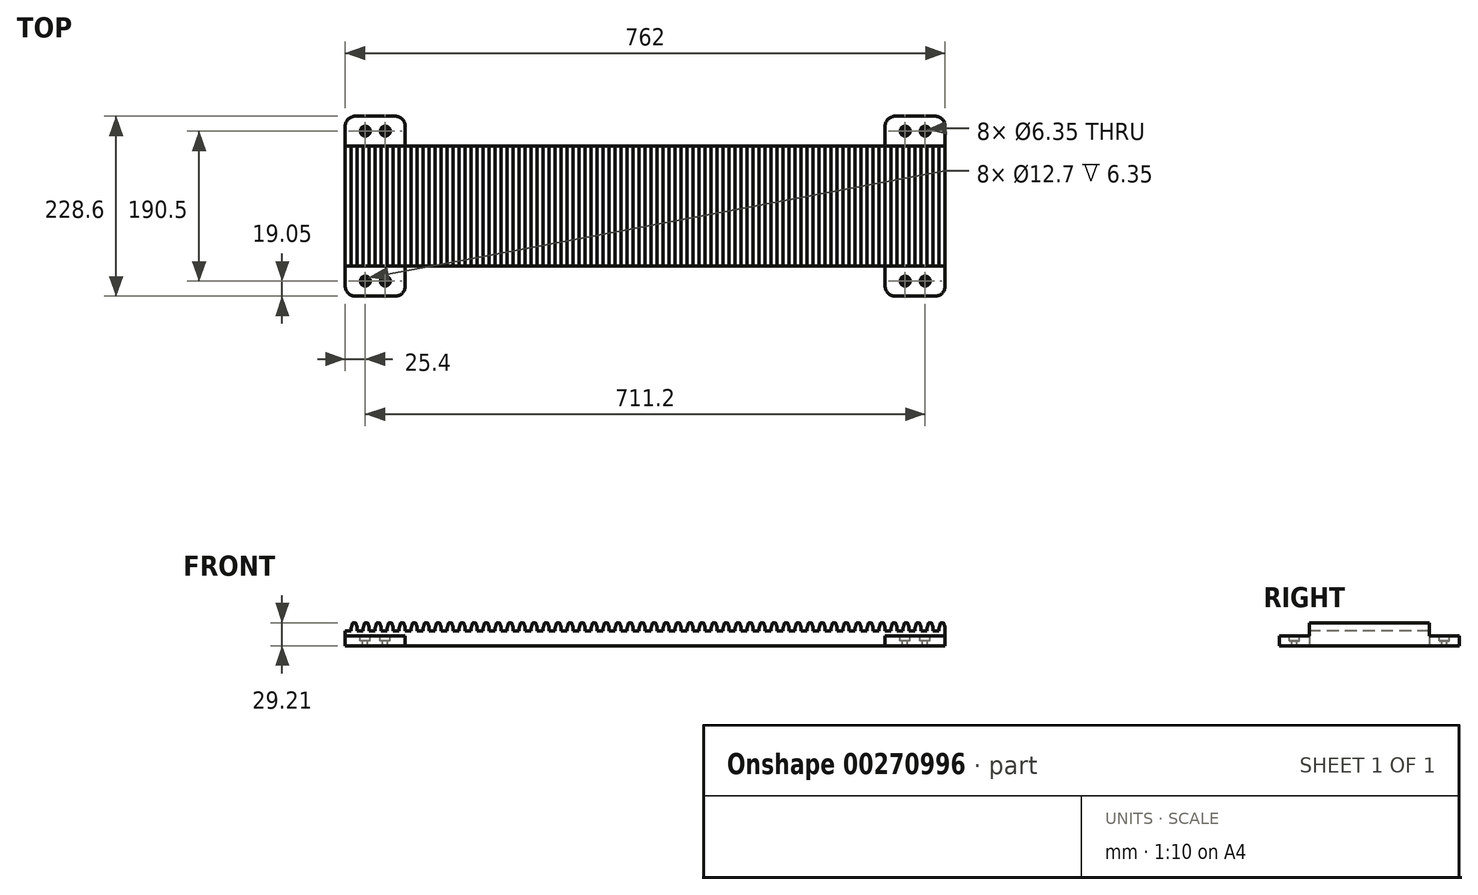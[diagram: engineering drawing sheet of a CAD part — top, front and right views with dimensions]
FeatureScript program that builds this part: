
annotation { "Feature Type Name" : "Feature", "Feature Type Description" : "" }
export const myFeature = defineFeature(function(context is Context, id is Id, definition is map)
    precondition{}
    {
        {
            var Q0;
            Q0=qCreatedBy(makeId("Top.planeOp"),FACE);
            var sketch = newSketch(context, id + "F0", { "sketchPlane" : qUnion([Q0])});
            skLineSegment(sketch, "E0", {"start": v(0, 12.7) * mm, "end": v(0, 215.9) * mm});
            skLineSegment(sketch, "E1", {"start": v(12.7, 228.6) * mm, "end": v(63.5, 228.6) * mm});
            skLineSegment(sketch, "E2", {"start": v(76.2, 215.9) * mm, "end": v(76.2, 190.5) * mm});
            skLineSegment(sketch, "E3", {"start": v(76.2, 190.5) * mm, "end": v(381, 190.5) * mm});
            skLineSegment(sketch, "E4", {"start": v(12.7, 0) * mm, "end": v(63.5, 0) * mm});
            skLineSegment(sketch, "E5", {"start": v(76.2, 12.7) * mm, "end": v(76.2, 38.1) * mm});
            skPoint(sketch, "E5.endSnap0", {"position": v(76.2, 209.55) * mm});
            skLineSegment(sketch, "E6", {"start": v(76.2, 38.1) * mm, "end": v(381, 38.1) * mm});
            skLineSegment(sketch, "E7", {"start": v(381, 190.5) * mm, "end": v(381, 38.1) * mm, "construction": true});
            skPoint(sketch, "E8.visualSharp", {"position": v(76.2, 228.6) * mm});
            skArc(sketch, "E8.filletArc", {"start": v(76.2, 215.9) * mm, "mid": v(72.48, 224.88) * mm, "end": v(63.5, 228.6) * mm});
            skPoint(sketch, "E9.visualSharp", {"position": v(0, 228.6) * mm});
            skArc(sketch, "E9.filletArc", {"start": v(12.7, 228.6) * mm, "mid": v(3.72, 224.88) * mm, "end": v(0, 215.9) * mm});
            skPoint(sketch, "E10.visualSharp", {"position": v(0, 0) * mm});
            skArc(sketch, "E10.filletArc", {"start": v(0, 12.7) * mm, "mid": v(3.72, 3.72) * mm, "end": v(12.7, 0) * mm});
            skPoint(sketch, "E11.visualSharp", {"position": v(76.2, 0) * mm});
            skArc(sketch, "E11.filletArc", {"start": v(63.5, 0) * mm, "mid": v(72.48, 3.72) * mm, "end": v(76.2, 12.7) * mm});
            skArc(sketch, "E12.MirrorCS", {"start": v(762, 12.7) * mm, "mid": v(758.28, 3.72) * mm, "end": v(749.3, 0) * mm});
            skArc(sketch, "E13.MirrorCS", {"start": v(749.3, 228.6) * mm, "mid": v(758.28, 224.88) * mm, "end": v(762, 215.9) * mm});
            skArc(sketch, "E14.MirrorCS", {"start": v(685.8, 215.9) * mm, "mid": v(689.52, 224.88) * mm, "end": v(698.5, 228.6) * mm});
            skArc(sketch, "E15.MirrorCS", {"start": v(698.5, 0) * mm, "mid": v(689.52, 3.72) * mm, "end": v(685.8, 12.7) * mm});
            skLineSegment(sketch, "E16.MirrorCS", {"start": v(685.8, 215.9) * mm, "end": v(685.8, 190.5) * mm});
            skPoint(sketch, "E17.MirrorP", {"position": v(685.8, 209.55) * mm});
            skPoint(sketch, "E18.MirrorP", {"position": v(685.8, 0) * mm});
            skLineSegment(sketch, "E19.MirrorCS", {"start": v(762, 12.7) * mm, "end": v(762, 215.9) * mm});
            skPoint(sketch, "E20.MirrorP", {"position": v(762, 228.6) * mm});
            skPoint(sketch, "E21.MirrorP", {"position": v(685.8, 228.6) * mm});
            skLineSegment(sketch, "E22.MirrorCS", {"start": v(749.3, 228.6) * mm, "end": v(698.5, 228.6) * mm});
            skPoint(sketch, "E23.MirrorP", {"position": v(762, 0) * mm});
            skLineSegment(sketch, "E24.MirrorCS", {"start": v(749.3, 0) * mm, "end": v(698.5, 0) * mm});
            skLineSegment(sketch, "E25.MirrorCS", {"start": v(685.8, 38.1) * mm, "end": v(381, 38.1) * mm});
            skLineSegment(sketch, "E26.MirrorCS", {"start": v(685.8, 190.5) * mm, "end": v(381, 190.5) * mm});
            skLineSegment(sketch, "E27.MirrorCS", {"start": v(685.8, 12.7) * mm, "end": v(685.8, 38.1) * mm});
            skPoint(sketch, "E28", {"position": v(25.4, 209.55) * mm});
            skPoint(sketch, "E29", {"position": v(50.8, 209.55) * mm});
            skLineSegment(sketch, "E30", {"start": v(0, 114.3) * mm, "end": v(762, 114.3) * mm, "construction": true});
            skPoint(sketch, "E31.MirrorP", {"position": v(50.8, 19.05) * mm});
            skPoint(sketch, "E32.MirrorP", {"position": v(25.4, 19.05) * mm});
            skPoint(sketch, "E33.MirrorP", {"position": v(736.6, 209.55) * mm});
            skPoint(sketch, "E34.MirrorP", {"position": v(711.2, 209.55) * mm});
            skPoint(sketch, "E35.MirrorP", {"position": v(711.2, 19.05) * mm});
            skPoint(sketch, "E36.MirrorP", {"position": v(736.6, 19.05) * mm});
            skSolve(sketch);
        }
        {
            var Q0;
            Q0 = qSketchRegion(id + "F0", true);
            extrude(context, id + "F1", {"entities" : qUnion([Q0]), "depth" : 12.7 * mm});
        }
        {
            var Q0;
            Q0=makeQuery(id+"F1.opExtrude","CAP_FACE",FACE,{"disambiguationData":[OSD([sQuery(id+"F0.wireOp",EDGE,"E0"),sQuery(id+"F0.wireOp",EDGE,"E1"),sQuery(id+"F0.wireOp",EDGE,"E2"),sQuery(id+"F0.wireOp",EDGE,"E3"),sQuery(id+"F0.wireOp",EDGE,"E4"),sQuery(id+"F0.wireOp",EDGE,"E5"),sQuery(id+"F0.wireOp",EDGE,"E6"),sQuery(id+"F0.wireOp",EDGE,"E8.filletArc"),sQuery(id+"F0.wireOp",EDGE,"E9.filletArc"),sQuery(id+"F0.wireOp",EDGE,"E10.filletArc"),sQuery(id+"F0.wireOp",EDGE,"E11.filletArc"),sQuery(id+"F0.wireOp",EDGE,"E12.MirrorCS"),sQuery(id+"F0.wireOp",EDGE,"E13.MirrorCS"),sQuery(id+"F0.wireOp",EDGE,"E14.MirrorCS"),sQuery(id+"F0.wireOp",EDGE,"E15.MirrorCS"),sQuery(id+"F0.wireOp",EDGE,"E16.MirrorCS"),sQuery(id+"F0.wireOp",EDGE,"E19.MirrorCS"),sQuery(id+"F0.wireOp",EDGE,"E22.MirrorCS"),sQuery(id+"F0.wireOp",EDGE,"E24.MirrorCS"),sQuery(id+"F0.wireOp",EDGE,"E25.MirrorCS"),sQuery(id+"F0.wireOp",EDGE,"E26.MirrorCS"),sQuery(id+"F0.wireOp",EDGE,"E27.MirrorCS")])],"isStart":false});
            var sketch = newSketch(context, id + "F2", { "sketchPlane" : qUnion([Q0])});
            skLineSegment(sketch, "E37", {"start": v(0, 190.5) * mm, "end": v(762, 190.5) * mm});
            skLineSegment(sketch, "E38", {"start": v(762, 190.5) * mm, "end": v(762, 38.1) * mm});
            skLineSegment(sketch, "E39", {"start": v(762, 38.1) * mm, "end": v(0, 38.1) * mm});
            skPoint(sketch, "E39.endSnap0", {"position": v(0, 114.3) * mm});
            skLineSegment(sketch, "E40", {"start": v(0, 38.1) * mm, "end": v(0, 190.5) * mm});
            skPoint(sketch, "E41", {"position": v(25.4, 209.55) * mm});
            skPoint(sketch, "E42", {"position": v(50.8, 209.55) * mm});
            skPoint(sketch, "E43.MirrorP", {"position": v(25.4, 19.05) * mm});
            skPoint(sketch, "E44.MirrorP", {"position": v(50.8, 19.05) * mm});
            skPoint(sketch, "E45.MirrorP", {"position": v(711.2, 209.55) * mm});
            skPoint(sketch, "E46.MirrorP", {"position": v(736.6, 209.55) * mm});
            skPoint(sketch, "E47.MirrorP", {"position": v(736.6, 19.05) * mm});
            skPoint(sketch, "E48.MirrorP", {"position": v(711.2, 19.05) * mm});
            skSolve(sketch);
        }
        {
            var Q0;
            Q0 = qSketchRegion(id + "F2", true);
            extrude(context, id + "F3", {"entities" : qUnion([Q0]), "operationType" : NewBodyOperationType.ADD, "depth" : 6.35 * mm});
        }
        {
            var Q0;
            Q0=sQuery(id+"F2.wireOp",VERTEX,"E46.MirrorP");
            var Q1;
            Q1=sQuery(id+"F2.wireOp",VERTEX,"E45.MirrorP");
            var Q2;
            Q2=sQuery(id+"F2.wireOp",VERTEX,"E47.MirrorP");
            var Q3;
            Q3=sQuery(id+"F2.wireOp",VERTEX,"E48.MirrorP");
            var Q4;
            Q4=sQuery(id+"F2.wireOp",VERTEX,"E42");
            var Q5;
            Q5=sQuery(id+"F2.wireOp",VERTEX,"E41");
            var Q6;
            Q6=sQuery(id+"F2.wireOp",VERTEX,"E44.MirrorP");
            var Q7;
            Q7=sQuery(id+"F2.wireOp",VERTEX,"E43.MirrorP");
            var Q8;
            Q8=makeQuery(id+"F1.opExtrude","SWEPT_BODY",BODY,{"disambiguationData":[OSD([sQuery(id+"F0.wireOp",EDGE,"E0"),sQuery(id+"F0.wireOp",EDGE,"E1"),sQuery(id+"F0.wireOp",EDGE,"E2"),sQuery(id+"F0.wireOp",EDGE,"E3"),sQuery(id+"F0.wireOp",EDGE,"E4"),sQuery(id+"F0.wireOp",EDGE,"E5"),sQuery(id+"F0.wireOp",EDGE,"E6"),sQuery(id+"F0.wireOp",EDGE,"E8.filletArc"),sQuery(id+"F0.wireOp",EDGE,"E9.filletArc"),sQuery(id+"F0.wireOp",EDGE,"E10.filletArc"),sQuery(id+"F0.wireOp",EDGE,"E11.filletArc"),sQuery(id+"F0.wireOp",EDGE,"E12.MirrorCS"),sQuery(id+"F0.wireOp",EDGE,"E13.MirrorCS"),sQuery(id+"F0.wireOp",EDGE,"E14.MirrorCS"),sQuery(id+"F0.wireOp",EDGE,"E15.MirrorCS"),sQuery(id+"F0.wireOp",EDGE,"E16.MirrorCS"),sQuery(id+"F0.wireOp",EDGE,"E19.MirrorCS"),sQuery(id+"F0.wireOp",EDGE,"E22.MirrorCS"),sQuery(id+"F0.wireOp",EDGE,"E24.MirrorCS"),sQuery(id+"F0.wireOp",EDGE,"E25.MirrorCS"),sQuery(id+"F0.wireOp",EDGE,"E26.MirrorCS"),sQuery(id+"F0.wireOp",EDGE,"E27.MirrorCS")])]});
            hole(context, id + "F4", {"style" : HoleStyle.C_BORE, "endStyle" : HoleEndStyle.THROUGH, "holeDiameter" : 6.35 * mm, "cBoreDiameter" : 12.7 * mm, "cBoreDepth" : 6.35 * mm, "tappedDepth" : 12.7 * mm, "tapClearance" : 3, "locations" : qUnion([Q0, Q1, Q2, Q3, Q4, Q5, Q6, Q7]), "scope" : qUnion([Q8])});
        }
        {
            var Q0;
            Q0=makeQuery(id+"F3.opExtrude","CAP_FACE",FACE,{"disambiguationData":[OSD([sQuery(id+"F2.wireOp",EDGE,"E37"),sQuery(id+"F2.wireOp",EDGE,"E38"),sQuery(id+"F2.wireOp",EDGE,"E39"),sQuery(id+"F2.wireOp",EDGE,"E40")])],"isStart":false});
            var sketch = newSketch(context, id + "F5", { "sketchPlane" : qUnion([Q0])});
            skLineSegment(sketch, "E49", {"start": v(7.62, 190.5) * mm, "end": v(7.62, 38.1) * mm});
            skLineSegment(sketch, "E50.0", {"start": v(15.24, 190.5) * mm, "end": v(15.24, 38.1) * mm});
            skLineSegment(sketch, "E51", {"start": v(15.24, 190.5) * mm, "end": v(7.62, 190.5) * mm});
            skLineSegment(sketch, "E52.0", {"start": v(22.86, 190.5) * mm, "end": v(22.86, 38.1) * mm});
            skLineSegment(sketch, "E53.0", {"start": v(30.48, 190.5) * mm, "end": v(30.48, 38.1) * mm});
            skLineSegment(sketch, "E54", {"start": v(22.86, 190.5) * mm, "end": v(30.48, 190.5) * mm});
            skLineSegment(sketch, "E55", {"start": v(22.86, 38.1) * mm, "end": v(30.48, 38.1) * mm});
            skLineSegment(sketch, "E56", {"start": v(7.62, 38.1) * mm, "end": v(15.24, 38.1) * mm});
            skLineSegment(sketch, "E57.1.0.0", {"start": v(45.72, 190.5) * mm, "end": v(38.1, 190.5) * mm});
            skLineSegment(sketch, "E57.1.0.1", {"start": v(38.1, 190.5) * mm, "end": v(38.1, 38.1) * mm});
            skLineSegment(sketch, "E57.1.0.2", {"start": v(45.72, 190.5) * mm, "end": v(45.72, 38.1) * mm});
            skLineSegment(sketch, "E57.1.0.3", {"start": v(53.34, 190.5) * mm, "end": v(53.34, 38.1) * mm});
            skLineSegment(sketch, "E57.1.0.4", {"start": v(53.34, 190.5) * mm, "end": v(60.96, 190.5) * mm});
            skLineSegment(sketch, "E57.1.0.5", {"start": v(60.96, 190.5) * mm, "end": v(60.96, 38.1) * mm});
            skLineSegment(sketch, "E57.1.0.6", {"start": v(53.34, 38.1) * mm, "end": v(60.96, 38.1) * mm});
            skLineSegment(sketch, "E57.1.0.7", {"start": v(38.1, 38.1) * mm, "end": v(45.72, 38.1) * mm});
            skLineSegment(sketch, "E57.2.0.0", {"start": v(76.2, 190.5) * mm, "end": v(68.58, 190.5) * mm});
            skLineSegment(sketch, "E57.2.0.1", {"start": v(68.58, 190.5) * mm, "end": v(68.58, 38.1) * mm});
            skLineSegment(sketch, "E57.2.0.2", {"start": v(76.2, 190.5) * mm, "end": v(76.2, 38.1) * mm});
            skLineSegment(sketch, "E57.2.0.3", {"start": v(83.82, 190.5) * mm, "end": v(83.82, 38.1) * mm});
            skLineSegment(sketch, "E57.2.0.4", {"start": v(83.82, 190.5) * mm, "end": v(91.44, 190.5) * mm});
            skLineSegment(sketch, "E57.2.0.5", {"start": v(91.44, 190.5) * mm, "end": v(91.44, 38.1) * mm});
            skLineSegment(sketch, "E57.2.0.6", {"start": v(83.82, 38.1) * mm, "end": v(91.44, 38.1) * mm});
            skLineSegment(sketch, "E57.2.0.7", {"start": v(68.58, 38.1) * mm, "end": v(76.2, 38.1) * mm});
            skLineSegment(sketch, "E57.3.0.0", {"start": v(106.68, 190.5) * mm, "end": v(99.06, 190.5) * mm});
            skLineSegment(sketch, "E57.3.0.1", {"start": v(99.06, 190.5) * mm, "end": v(99.06, 38.1) * mm});
            skLineSegment(sketch, "E57.3.0.2", {"start": v(106.68, 190.5) * mm, "end": v(106.68, 38.1) * mm});
            skLineSegment(sketch, "E57.3.0.3", {"start": v(114.3, 190.5) * mm, "end": v(114.3, 38.1) * mm});
            skLineSegment(sketch, "E57.3.0.4", {"start": v(114.3, 190.5) * mm, "end": v(121.92, 190.5) * mm});
            skLineSegment(sketch, "E57.3.0.5", {"start": v(121.92, 190.5) * mm, "end": v(121.92, 38.1) * mm});
            skLineSegment(sketch, "E57.3.0.6", {"start": v(114.3, 38.1) * mm, "end": v(121.92, 38.1) * mm});
            skLineSegment(sketch, "E57.3.0.7", {"start": v(99.06, 38.1) * mm, "end": v(106.68, 38.1) * mm});
            skLineSegment(sketch, "E57.4.0.0", {"start": v(137.16, 190.5) * mm, "end": v(129.54, 190.5) * mm});
            skLineSegment(sketch, "E57.4.0.1", {"start": v(129.54, 190.5) * mm, "end": v(129.54, 38.1) * mm});
            skLineSegment(sketch, "E57.4.0.2", {"start": v(137.16, 190.5) * mm, "end": v(137.16, 38.1) * mm});
            skLineSegment(sketch, "E57.4.0.3", {"start": v(144.78, 190.5) * mm, "end": v(144.78, 38.1) * mm});
            skLineSegment(sketch, "E57.4.0.4", {"start": v(144.78, 190.5) * mm, "end": v(152.4, 190.5) * mm});
            skLineSegment(sketch, "E57.4.0.5", {"start": v(152.4, 190.5) * mm, "end": v(152.4, 38.1) * mm});
            skLineSegment(sketch, "E57.4.0.6", {"start": v(144.78, 38.1) * mm, "end": v(152.4, 38.1) * mm});
            skLineSegment(sketch, "E57.4.0.7", {"start": v(129.54, 38.1) * mm, "end": v(137.16, 38.1) * mm});
            skLineSegment(sketch, "E57.5.0.0", {"start": v(167.64, 190.5) * mm, "end": v(160.02, 190.5) * mm});
            skLineSegment(sketch, "E57.5.0.1", {"start": v(160.02, 190.5) * mm, "end": v(160.02, 38.1) * mm});
            skLineSegment(sketch, "E57.5.0.2", {"start": v(167.64, 190.5) * mm, "end": v(167.64, 38.1) * mm});
            skLineSegment(sketch, "E57.5.0.3", {"start": v(175.26, 190.5) * mm, "end": v(175.26, 38.1) * mm});
            skLineSegment(sketch, "E57.5.0.4", {"start": v(175.26, 190.5) * mm, "end": v(182.88, 190.5) * mm});
            skLineSegment(sketch, "E57.5.0.5", {"start": v(182.88, 190.5) * mm, "end": v(182.88, 38.1) * mm});
            skLineSegment(sketch, "E57.5.0.6", {"start": v(175.26, 38.1) * mm, "end": v(182.88, 38.1) * mm});
            skLineSegment(sketch, "E57.5.0.7", {"start": v(160.02, 38.1) * mm, "end": v(167.64, 38.1) * mm});
            skLineSegment(sketch, "E57.6.0.0", {"start": v(198.12, 190.5) * mm, "end": v(190.5, 190.5) * mm});
            skLineSegment(sketch, "E57.6.0.1", {"start": v(190.5, 190.5) * mm, "end": v(190.5, 38.1) * mm});
            skLineSegment(sketch, "E57.6.0.2", {"start": v(198.12, 190.5) * mm, "end": v(198.12, 38.1) * mm});
            skLineSegment(sketch, "E57.6.0.3", {"start": v(205.74, 190.5) * mm, "end": v(205.74, 38.1) * mm});
            skLineSegment(sketch, "E57.6.0.4", {"start": v(205.74, 190.5) * mm, "end": v(213.36, 190.5) * mm});
            skLineSegment(sketch, "E57.6.0.5", {"start": v(213.36, 190.5) * mm, "end": v(213.36, 38.1) * mm});
            skLineSegment(sketch, "E57.6.0.6", {"start": v(205.74, 38.1) * mm, "end": v(213.36, 38.1) * mm});
            skLineSegment(sketch, "E57.6.0.7", {"start": v(190.5, 38.1) * mm, "end": v(198.12, 38.1) * mm});
            skLineSegment(sketch, "E57.7.0.0", {"start": v(228.6, 190.5) * mm, "end": v(220.98, 190.5) * mm});
            skLineSegment(sketch, "E57.7.0.1", {"start": v(220.98, 190.5) * mm, "end": v(220.98, 38.1) * mm});
            skLineSegment(sketch, "E57.7.0.2", {"start": v(228.6, 190.5) * mm, "end": v(228.6, 38.1) * mm});
            skLineSegment(sketch, "E57.7.0.3", {"start": v(236.22, 190.5) * mm, "end": v(236.22, 38.1) * mm});
            skLineSegment(sketch, "E57.7.0.4", {"start": v(236.22, 190.5) * mm, "end": v(243.84, 190.5) * mm});
            skLineSegment(sketch, "E57.7.0.5", {"start": v(243.84, 190.5) * mm, "end": v(243.84, 38.1) * mm});
            skLineSegment(sketch, "E57.7.0.6", {"start": v(236.22, 38.1) * mm, "end": v(243.84, 38.1) * mm});
            skLineSegment(sketch, "E57.7.0.7", {"start": v(220.98, 38.1) * mm, "end": v(228.6, 38.1) * mm});
            skLineSegment(sketch, "E57.8.0.0", {"start": v(259.08, 190.5) * mm, "end": v(251.46, 190.5) * mm});
            skLineSegment(sketch, "E57.8.0.1", {"start": v(251.46, 190.5) * mm, "end": v(251.46, 38.1) * mm});
            skLineSegment(sketch, "E57.8.0.2", {"start": v(259.08, 190.5) * mm, "end": v(259.08, 38.1) * mm});
            skLineSegment(sketch, "E57.8.0.3", {"start": v(266.7, 190.5) * mm, "end": v(266.7, 38.1) * mm});
            skLineSegment(sketch, "E57.8.0.4", {"start": v(266.7, 190.5) * mm, "end": v(274.32, 190.5) * mm});
            skLineSegment(sketch, "E57.8.0.5", {"start": v(274.32, 190.5) * mm, "end": v(274.32, 38.1) * mm});
            skLineSegment(sketch, "E57.8.0.6", {"start": v(266.7, 38.1) * mm, "end": v(274.32, 38.1) * mm});
            skLineSegment(sketch, "E57.8.0.7", {"start": v(251.46, 38.1) * mm, "end": v(259.08, 38.1) * mm});
            skLineSegment(sketch, "E57.9.0.0", {"start": v(289.56, 190.5) * mm, "end": v(281.94, 190.5) * mm});
            skLineSegment(sketch, "E57.9.0.1", {"start": v(281.94, 190.5) * mm, "end": v(281.94, 38.1) * mm});
            skLineSegment(sketch, "E57.9.0.2", {"start": v(289.56, 190.5) * mm, "end": v(289.56, 38.1) * mm});
            skLineSegment(sketch, "E57.9.0.3", {"start": v(297.18, 190.5) * mm, "end": v(297.18, 38.1) * mm});
            skLineSegment(sketch, "E57.9.0.4", {"start": v(297.18, 190.5) * mm, "end": v(304.8, 190.5) * mm});
            skLineSegment(sketch, "E57.9.0.5", {"start": v(304.8, 190.5) * mm, "end": v(304.8, 38.1) * mm});
            skLineSegment(sketch, "E57.9.0.6", {"start": v(297.18, 38.1) * mm, "end": v(304.8, 38.1) * mm});
            skLineSegment(sketch, "E57.9.0.7", {"start": v(281.94, 38.1) * mm, "end": v(289.56, 38.1) * mm});
            skLineSegment(sketch, "E57.10.0.0", {"start": v(320.04, 190.5) * mm, "end": v(312.42, 190.5) * mm});
            skLineSegment(sketch, "E57.10.0.1", {"start": v(312.42, 190.5) * mm, "end": v(312.42, 38.1) * mm});
            skLineSegment(sketch, "E57.10.0.2", {"start": v(320.04, 190.5) * mm, "end": v(320.04, 38.1) * mm});
            skLineSegment(sketch, "E57.10.0.3", {"start": v(327.66, 190.5) * mm, "end": v(327.66, 38.1) * mm});
            skLineSegment(sketch, "E57.10.0.4", {"start": v(327.66, 190.5) * mm, "end": v(335.28, 190.5) * mm});
            skLineSegment(sketch, "E57.10.0.5", {"start": v(335.28, 190.5) * mm, "end": v(335.28, 38.1) * mm});
            skLineSegment(sketch, "E57.10.0.6", {"start": v(327.66, 38.1) * mm, "end": v(335.28, 38.1) * mm});
            skLineSegment(sketch, "E57.10.0.7", {"start": v(312.42, 38.1) * mm, "end": v(320.04, 38.1) * mm});
            skLineSegment(sketch, "E57.11.0.0", {"start": v(350.52, 190.5) * mm, "end": v(342.9, 190.5) * mm});
            skLineSegment(sketch, "E57.11.0.1", {"start": v(342.9, 190.5) * mm, "end": v(342.9, 38.1) * mm});
            skLineSegment(sketch, "E57.11.0.2", {"start": v(350.52, 190.5) * mm, "end": v(350.52, 38.1) * mm});
            skLineSegment(sketch, "E57.11.0.3", {"start": v(358.14, 190.5) * mm, "end": v(358.14, 38.1) * mm});
            skLineSegment(sketch, "E57.11.0.4", {"start": v(358.14, 190.5) * mm, "end": v(365.76, 190.5) * mm});
            skLineSegment(sketch, "E57.11.0.5", {"start": v(365.76, 190.5) * mm, "end": v(365.76, 38.1) * mm});
            skLineSegment(sketch, "E57.11.0.6", {"start": v(358.14, 38.1) * mm, "end": v(365.76, 38.1) * mm});
            skLineSegment(sketch, "E57.11.0.7", {"start": v(342.9, 38.1) * mm, "end": v(350.52, 38.1) * mm});
            skLineSegment(sketch, "E57.12.0.0", {"start": v(381, 190.5) * mm, "end": v(373.38, 190.5) * mm});
            skLineSegment(sketch, "E57.12.0.1", {"start": v(373.38, 190.5) * mm, "end": v(373.38, 38.1) * mm});
            skLineSegment(sketch, "E57.12.0.2", {"start": v(381, 190.5) * mm, "end": v(381, 38.1) * mm});
            skLineSegment(sketch, "E57.12.0.3", {"start": v(388.62, 190.5) * mm, "end": v(388.62, 38.1) * mm});
            skLineSegment(sketch, "E57.12.0.4", {"start": v(388.62, 190.5) * mm, "end": v(396.24, 190.5) * mm});
            skLineSegment(sketch, "E57.12.0.5", {"start": v(396.24, 190.5) * mm, "end": v(396.24, 38.1) * mm});
            skLineSegment(sketch, "E57.12.0.6", {"start": v(388.62, 38.1) * mm, "end": v(396.24, 38.1) * mm});
            skLineSegment(sketch, "E57.12.0.7", {"start": v(373.38, 38.1) * mm, "end": v(381, 38.1) * mm});
            skLineSegment(sketch, "E57.13.0.0", {"start": v(411.48, 190.5) * mm, "end": v(403.86, 190.5) * mm});
            skLineSegment(sketch, "E57.13.0.1", {"start": v(403.86, 190.5) * mm, "end": v(403.86, 38.1) * mm});
            skLineSegment(sketch, "E57.13.0.2", {"start": v(411.48, 190.5) * mm, "end": v(411.48, 38.1) * mm});
            skLineSegment(sketch, "E57.13.0.3", {"start": v(419.1, 190.5) * mm, "end": v(419.1, 38.1) * mm});
            skLineSegment(sketch, "E57.13.0.4", {"start": v(419.1, 190.5) * mm, "end": v(426.72, 190.5) * mm});
            skLineSegment(sketch, "E57.13.0.5", {"start": v(426.72, 190.5) * mm, "end": v(426.72, 38.1) * mm});
            skLineSegment(sketch, "E57.13.0.6", {"start": v(419.1, 38.1) * mm, "end": v(426.72, 38.1) * mm});
            skLineSegment(sketch, "E57.13.0.7", {"start": v(403.86, 38.1) * mm, "end": v(411.48, 38.1) * mm});
            skLineSegment(sketch, "E57.14.0.0", {"start": v(441.96, 190.5) * mm, "end": v(434.34, 190.5) * mm});
            skLineSegment(sketch, "E57.14.0.1", {"start": v(434.34, 190.5) * mm, "end": v(434.34, 38.1) * mm});
            skLineSegment(sketch, "E57.14.0.2", {"start": v(441.96, 190.5) * mm, "end": v(441.96, 38.1) * mm});
            skLineSegment(sketch, "E57.14.0.3", {"start": v(449.58, 190.5) * mm, "end": v(449.58, 38.1) * mm});
            skLineSegment(sketch, "E57.14.0.4", {"start": v(449.58, 190.5) * mm, "end": v(457.2, 190.5) * mm});
            skLineSegment(sketch, "E57.14.0.5", {"start": v(457.2, 190.5) * mm, "end": v(457.2, 38.1) * mm});
            skLineSegment(sketch, "E57.14.0.6", {"start": v(449.58, 38.1) * mm, "end": v(457.2, 38.1) * mm});
            skLineSegment(sketch, "E57.14.0.7", {"start": v(434.34, 38.1) * mm, "end": v(441.96, 38.1) * mm});
            skLineSegment(sketch, "E57.15.0.0", {"start": v(472.44, 190.5) * mm, "end": v(464.82, 190.5) * mm});
            skLineSegment(sketch, "E57.15.0.1", {"start": v(464.82, 190.5) * mm, "end": v(464.82, 38.1) * mm});
            skLineSegment(sketch, "E57.15.0.2", {"start": v(472.44, 190.5) * mm, "end": v(472.44, 38.1) * mm});
            skLineSegment(sketch, "E57.15.0.3", {"start": v(480.06, 190.5) * mm, "end": v(480.06, 38.1) * mm});
            skLineSegment(sketch, "E57.15.0.4", {"start": v(480.06, 190.5) * mm, "end": v(487.68, 190.5) * mm});
            skLineSegment(sketch, "E57.15.0.5", {"start": v(487.68, 190.5) * mm, "end": v(487.68, 38.1) * mm});
            skLineSegment(sketch, "E57.15.0.6", {"start": v(480.06, 38.1) * mm, "end": v(487.68, 38.1) * mm});
            skLineSegment(sketch, "E57.15.0.7", {"start": v(464.82, 38.1) * mm, "end": v(472.44, 38.1) * mm});
            skLineSegment(sketch, "E57.16.0.0", {"start": v(502.92, 190.5) * mm, "end": v(495.3, 190.5) * mm});
            skLineSegment(sketch, "E57.16.0.1", {"start": v(495.3, 190.5) * mm, "end": v(495.3, 38.1) * mm});
            skLineSegment(sketch, "E57.16.0.2", {"start": v(502.92, 190.5) * mm, "end": v(502.92, 38.1) * mm});
            skLineSegment(sketch, "E57.16.0.3", {"start": v(510.54, 190.5) * mm, "end": v(510.54, 38.1) * mm});
            skLineSegment(sketch, "E57.16.0.4", {"start": v(510.54, 190.5) * mm, "end": v(518.16, 190.5) * mm});
            skLineSegment(sketch, "E57.16.0.5", {"start": v(518.16, 190.5) * mm, "end": v(518.16, 38.1) * mm});
            skLineSegment(sketch, "E57.16.0.6", {"start": v(510.54, 38.1) * mm, "end": v(518.16, 38.1) * mm});
            skLineSegment(sketch, "E57.16.0.7", {"start": v(495.3, 38.1) * mm, "end": v(502.92, 38.1) * mm});
            skLineSegment(sketch, "E57.17.0.0", {"start": v(533.4, 190.5) * mm, "end": v(525.78, 190.5) * mm});
            skLineSegment(sketch, "E57.17.0.1", {"start": v(525.78, 190.5) * mm, "end": v(525.78, 38.1) * mm});
            skLineSegment(sketch, "E57.17.0.2", {"start": v(533.4, 190.5) * mm, "end": v(533.4, 38.1) * mm});
            skLineSegment(sketch, "E57.17.0.3", {"start": v(541.02, 190.5) * mm, "end": v(541.02, 38.1) * mm});
            skLineSegment(sketch, "E57.17.0.4", {"start": v(541.02, 190.5) * mm, "end": v(548.64, 190.5) * mm});
            skLineSegment(sketch, "E57.17.0.5", {"start": v(548.64, 190.5) * mm, "end": v(548.64, 38.1) * mm});
            skLineSegment(sketch, "E57.17.0.6", {"start": v(541.02, 38.1) * mm, "end": v(548.64, 38.1) * mm});
            skLineSegment(sketch, "E57.17.0.7", {"start": v(525.78, 38.1) * mm, "end": v(533.4, 38.1) * mm});
            skLineSegment(sketch, "E57.18.0.0", {"start": v(563.88, 190.5) * mm, "end": v(556.26, 190.5) * mm});
            skLineSegment(sketch, "E57.18.0.1", {"start": v(556.26, 190.5) * mm, "end": v(556.26, 38.1) * mm});
            skLineSegment(sketch, "E57.18.0.2", {"start": v(563.88, 190.5) * mm, "end": v(563.88, 38.1) * mm});
            skLineSegment(sketch, "E57.18.0.3", {"start": v(571.5, 190.5) * mm, "end": v(571.5, 38.1) * mm});
            skLineSegment(sketch, "E57.18.0.4", {"start": v(571.5, 190.5) * mm, "end": v(579.12, 190.5) * mm});
            skLineSegment(sketch, "E57.18.0.5", {"start": v(579.12, 190.5) * mm, "end": v(579.12, 38.1) * mm});
            skLineSegment(sketch, "E57.18.0.6", {"start": v(571.5, 38.1) * mm, "end": v(579.12, 38.1) * mm});
            skLineSegment(sketch, "E57.18.0.7", {"start": v(556.26, 38.1) * mm, "end": v(563.88, 38.1) * mm});
            skLineSegment(sketch, "E57.19.0.0", {"start": v(594.36, 190.5) * mm, "end": v(586.74, 190.5) * mm});
            skLineSegment(sketch, "E57.19.0.1", {"start": v(586.74, 190.5) * mm, "end": v(586.74, 38.1) * mm});
            skLineSegment(sketch, "E57.19.0.2", {"start": v(594.36, 190.5) * mm, "end": v(594.36, 38.1) * mm});
            skLineSegment(sketch, "E57.19.0.3", {"start": v(601.98, 190.5) * mm, "end": v(601.98, 38.1) * mm});
            skLineSegment(sketch, "E57.19.0.4", {"start": v(601.98, 190.5) * mm, "end": v(609.6, 190.5) * mm});
            skLineSegment(sketch, "E57.19.0.5", {"start": v(609.6, 190.5) * mm, "end": v(609.6, 38.1) * mm});
            skLineSegment(sketch, "E57.19.0.6", {"start": v(601.98, 38.1) * mm, "end": v(609.6, 38.1) * mm});
            skLineSegment(sketch, "E57.19.0.7", {"start": v(586.74, 38.1) * mm, "end": v(594.36, 38.1) * mm});
            skLineSegment(sketch, "E57.20.0.0", {"start": v(624.84, 190.5) * mm, "end": v(617.22, 190.5) * mm});
            skLineSegment(sketch, "E57.20.0.1", {"start": v(617.22, 190.5) * mm, "end": v(617.22, 38.1) * mm});
            skLineSegment(sketch, "E57.20.0.2", {"start": v(624.84, 190.5) * mm, "end": v(624.84, 38.1) * mm});
            skLineSegment(sketch, "E57.20.0.3", {"start": v(632.46, 190.5) * mm, "end": v(632.46, 38.1) * mm});
            skLineSegment(sketch, "E57.20.0.4", {"start": v(632.46, 190.5) * mm, "end": v(640.08, 190.5) * mm});
            skLineSegment(sketch, "E57.20.0.5", {"start": v(640.08, 190.5) * mm, "end": v(640.08, 38.1) * mm});
            skLineSegment(sketch, "E57.20.0.6", {"start": v(632.46, 38.1) * mm, "end": v(640.08, 38.1) * mm});
            skLineSegment(sketch, "E57.20.0.7", {"start": v(617.22, 38.1) * mm, "end": v(624.84, 38.1) * mm});
            skLineSegment(sketch, "E57.21.0.0", {"start": v(655.32, 190.5) * mm, "end": v(647.7, 190.5) * mm});
            skLineSegment(sketch, "E57.21.0.1", {"start": v(647.7, 190.5) * mm, "end": v(647.7, 38.1) * mm});
            skLineSegment(sketch, "E57.21.0.2", {"start": v(655.32, 190.5) * mm, "end": v(655.32, 38.1) * mm});
            skLineSegment(sketch, "E57.21.0.3", {"start": v(662.94, 190.5) * mm, "end": v(662.94, 38.1) * mm});
            skLineSegment(sketch, "E57.21.0.4", {"start": v(662.94, 190.5) * mm, "end": v(670.56, 190.5) * mm});
            skLineSegment(sketch, "E57.21.0.5", {"start": v(670.56, 190.5) * mm, "end": v(670.56, 38.1) * mm});
            skLineSegment(sketch, "E57.21.0.6", {"start": v(662.94, 38.1) * mm, "end": v(670.56, 38.1) * mm});
            skLineSegment(sketch, "E57.21.0.7", {"start": v(647.7, 38.1) * mm, "end": v(655.32, 38.1) * mm});
            skLineSegment(sketch, "E57.22.0.0", {"start": v(685.8, 190.5) * mm, "end": v(678.18, 190.5) * mm});
            skLineSegment(sketch, "E57.22.0.1", {"start": v(678.18, 190.5) * mm, "end": v(678.18, 38.1) * mm});
            skLineSegment(sketch, "E57.22.0.2", {"start": v(685.8, 190.5) * mm, "end": v(685.8, 38.1) * mm});
            skLineSegment(sketch, "E57.22.0.3", {"start": v(693.42, 190.5) * mm, "end": v(693.42, 38.1) * mm});
            skLineSegment(sketch, "E57.22.0.4", {"start": v(693.42, 190.5) * mm, "end": v(701.04, 190.5) * mm});
            skLineSegment(sketch, "E57.22.0.5", {"start": v(701.04, 190.5) * mm, "end": v(701.04, 38.1) * mm});
            skLineSegment(sketch, "E57.22.0.6", {"start": v(693.42, 38.1) * mm, "end": v(701.04, 38.1) * mm});
            skLineSegment(sketch, "E57.22.0.7", {"start": v(678.18, 38.1) * mm, "end": v(685.8, 38.1) * mm});
            skLineSegment(sketch, "E57.23.0.0", {"start": v(716.28, 190.5) * mm, "end": v(708.66, 190.5) * mm});
            skLineSegment(sketch, "E57.23.0.1", {"start": v(708.66, 190.5) * mm, "end": v(708.66, 38.1) * mm});
            skLineSegment(sketch, "E57.23.0.2", {"start": v(716.28, 190.5) * mm, "end": v(716.28, 38.1) * mm});
            skLineSegment(sketch, "E57.23.0.3", {"start": v(723.9, 190.5) * mm, "end": v(723.9, 38.1) * mm});
            skLineSegment(sketch, "E57.23.0.4", {"start": v(723.9, 190.5) * mm, "end": v(731.52, 190.5) * mm});
            skLineSegment(sketch, "E57.23.0.5", {"start": v(731.52, 190.5) * mm, "end": v(731.52, 38.1) * mm});
            skLineSegment(sketch, "E57.23.0.6", {"start": v(723.9, 38.1) * mm, "end": v(731.52, 38.1) * mm});
            skLineSegment(sketch, "E57.23.0.7", {"start": v(708.66, 38.1) * mm, "end": v(716.28, 38.1) * mm});
            skLineSegment(sketch, "E57.24.0.0", {"start": v(746.76, 190.5) * mm, "end": v(739.14, 190.5) * mm});
            skLineSegment(sketch, "E57.24.0.1", {"start": v(739.14, 190.5) * mm, "end": v(739.14, 38.1) * mm});
            skLineSegment(sketch, "E57.24.0.2", {"start": v(746.76, 190.5) * mm, "end": v(746.76, 38.1) * mm});
            skLineSegment(sketch, "E57.24.0.3", {"start": v(754.38, 190.5) * mm, "end": v(754.38, 38.1) * mm});
            skLineSegment(sketch, "E57.24.0.4", {"start": v(754.38, 190.5) * mm, "end": v(762, 190.5) * mm});
            skLineSegment(sketch, "E57.24.0.5", {"start": v(762, 190.5) * mm, "end": v(762, 38.1) * mm});
            skLineSegment(sketch, "E57.24.0.6", {"start": v(754.38, 38.1) * mm, "end": v(762, 38.1) * mm});
            skLineSegment(sketch, "E57.24.0.7", {"start": v(739.14, 38.1) * mm, "end": v(746.76, 38.1) * mm});
            skLineSegment(sketch, "E57.direction1", {"start": v(7.62, 190.5) * mm, "end": v(38.1, 190.5) * mm, "construction": true});
            skSolve(sketch);
        }
        {
            var Q0;
            Q0=makeQuery(id+"Fu1y5GcWRBi5nUe_1.boolean.opBoolean","MERGE",FACE,{"derivedFrom":[makeQuery(id+"F3.boolean.opBoolean","MERGE",FACE,{"derivedFrom":[makeQuery(id+"F1.opExtrude","SWEPT_FACE",FACE,{"disambiguationData":[OSD([sQuery(id+"F0.wireOp",EDGE,"E6"),sQuery(id+"F0.wireOp",EDGE,"E25.MirrorCS")])]}),makeQuery(id+"F3.opExtrude","SWEPT_FACE",FACE,{"disambiguationData":[OSD([sQuery(id+"F2.wireOp",EDGE,"E39")])]})]}),makeQuery(id+"Fu1y5GcWRBi5nUe_1.opExtrude","SWEPT_FACE",FACE,{"disambiguationData":[OSD([sQuery(id+"F5.wireOp",EDGE,"E55")])]}),makeQuery(id+"Fu1y5GcWRBi5nUe_1.opExtrude","SWEPT_FACE",FACE,{"disambiguationData":[OSD([sQuery(id+"F5.wireOp",EDGE,"E56")])]}),makeQuery(id+"Fu1y5GcWRBi5nUe_1.opExtrude","SWEPT_FACE",FACE,{"disambiguationData":[OSD([sQuery(id+"F5.wireOp",EDGE,"E57.1.0.6")])]}),makeQuery(id+"Fu1y5GcWRBi5nUe_1.opExtrude","SWEPT_FACE",FACE,{"disambiguationData":[OSD([sQuery(id+"F5.wireOp",EDGE,"E57.1.0.7")])]}),makeQuery(id+"Fu1y5GcWRBi5nUe_1.opExtrude","SWEPT_FACE",FACE,{"disambiguationData":[OSD([sQuery(id+"F5.wireOp",EDGE,"E57.2.0.6")])]}),makeQuery(id+"Fu1y5GcWRBi5nUe_1.opExtrude","SWEPT_FACE",FACE,{"disambiguationData":[OSD([sQuery(id+"F5.wireOp",EDGE,"E57.2.0.7")])]}),makeQuery(id+"Fu1y5GcWRBi5nUe_1.opExtrude","SWEPT_FACE",FACE,{"disambiguationData":[OSD([sQuery(id+"F5.wireOp",EDGE,"E57.3.0.6")])]}),makeQuery(id+"Fu1y5GcWRBi5nUe_1.opExtrude","SWEPT_FACE",FACE,{"disambiguationData":[OSD([sQuery(id+"F5.wireOp",EDGE,"E57.3.0.7")])]}),makeQuery(id+"Fu1y5GcWRBi5nUe_1.opExtrude","SWEPT_FACE",FACE,{"disambiguationData":[OSD([sQuery(id+"F5.wireOp",EDGE,"E57.4.0.6")])]}),makeQuery(id+"Fu1y5GcWRBi5nUe_1.opExtrude","SWEPT_FACE",FACE,{"disambiguationData":[OSD([sQuery(id+"F5.wireOp",EDGE,"E57.4.0.7")])]}),makeQuery(id+"Fu1y5GcWRBi5nUe_1.opExtrude","SWEPT_FACE",FACE,{"disambiguationData":[OSD([sQuery(id+"F5.wireOp",EDGE,"E57.5.0.6")])]}),makeQuery(id+"Fu1y5GcWRBi5nUe_1.opExtrude","SWEPT_FACE",FACE,{"disambiguationData":[OSD([sQuery(id+"F5.wireOp",EDGE,"E57.5.0.7")])]}),makeQuery(id+"Fu1y5GcWRBi5nUe_1.opExtrude","SWEPT_FACE",FACE,{"disambiguationData":[OSD([sQuery(id+"F5.wireOp",EDGE,"E57.6.0.6")])]}),makeQuery(id+"Fu1y5GcWRBi5nUe_1.opExtrude","SWEPT_FACE",FACE,{"disambiguationData":[OSD([sQuery(id+"F5.wireOp",EDGE,"E57.6.0.7")])]}),makeQuery(id+"Fu1y5GcWRBi5nUe_1.opExtrude","SWEPT_FACE",FACE,{"disambiguationData":[OSD([sQuery(id+"F5.wireOp",EDGE,"E57.7.0.6")])]}),makeQuery(id+"Fu1y5GcWRBi5nUe_1.opExtrude","SWEPT_FACE",FACE,{"disambiguationData":[OSD([sQuery(id+"F5.wireOp",EDGE,"E57.7.0.7")])]}),makeQuery(id+"Fu1y5GcWRBi5nUe_1.opExtrude","SWEPT_FACE",FACE,{"disambiguationData":[OSD([sQuery(id+"F5.wireOp",EDGE,"E57.8.0.6")])]}),makeQuery(id+"Fu1y5GcWRBi5nUe_1.opExtrude","SWEPT_FACE",FACE,{"disambiguationData":[OSD([sQuery(id+"F5.wireOp",EDGE,"E57.8.0.7")])]}),makeQuery(id+"Fu1y5GcWRBi5nUe_1.opExtrude","SWEPT_FACE",FACE,{"disambiguationData":[OSD([sQuery(id+"F5.wireOp",EDGE,"E57.9.0.6")])]}),makeQuery(id+"Fu1y5GcWRBi5nUe_1.opExtrude","SWEPT_FACE",FACE,{"disambiguationData":[OSD([sQuery(id+"F5.wireOp",EDGE,"E57.9.0.7")])]}),makeQuery(id+"Fu1y5GcWRBi5nUe_1.opExtrude","SWEPT_FACE",FACE,{"disambiguationData":[OSD([sQuery(id+"F5.wireOp",EDGE,"E57.10.0.6")])]}),makeQuery(id+"Fu1y5GcWRBi5nUe_1.opExtrude","SWEPT_FACE",FACE,{"disambiguationData":[OSD([sQuery(id+"F5.wireOp",EDGE,"E57.10.0.7")])]}),makeQuery(id+"Fu1y5GcWRBi5nUe_1.opExtrude","SWEPT_FACE",FACE,{"disambiguationData":[OSD([sQuery(id+"F5.wireOp",EDGE,"E57.11.0.6")])]}),makeQuery(id+"Fu1y5GcWRBi5nUe_1.opExtrude","SWEPT_FACE",FACE,{"disambiguationData":[OSD([sQuery(id+"F5.wireOp",EDGE,"E57.11.0.7")])]}),makeQuery(id+"Fu1y5GcWRBi5nUe_1.opExtrude","SWEPT_FACE",FACE,{"disambiguationData":[OSD([sQuery(id+"F5.wireOp",EDGE,"E57.12.0.6")])]}),makeQuery(id+"Fu1y5GcWRBi5nUe_1.opExtrude","SWEPT_FACE",FACE,{"disambiguationData":[OSD([sQuery(id+"F5.wireOp",EDGE,"E57.12.0.7")])]}),makeQuery(id+"Fu1y5GcWRBi5nUe_1.opExtrude","SWEPT_FACE",FACE,{"disambiguationData":[OSD([sQuery(id+"F5.wireOp",EDGE,"E57.13.0.6")])]}),makeQuery(id+"Fu1y5GcWRBi5nUe_1.opExtrude","SWEPT_FACE",FACE,{"disambiguationData":[OSD([sQuery(id+"F5.wireOp",EDGE,"E57.13.0.7")])]}),makeQuery(id+"Fu1y5GcWRBi5nUe_1.opExtrude","SWEPT_FACE",FACE,{"disambiguationData":[OSD([sQuery(id+"F5.wireOp",EDGE,"E57.14.0.6")])]}),makeQuery(id+"Fu1y5GcWRBi5nUe_1.opExtrude","SWEPT_FACE",FACE,{"disambiguationData":[OSD([sQuery(id+"F5.wireOp",EDGE,"E57.14.0.7")])]}),makeQuery(id+"Fu1y5GcWRBi5nUe_1.opExtrude","SWEPT_FACE",FACE,{"disambiguationData":[OSD([sQuery(id+"F5.wireOp",EDGE,"E57.15.0.6")])]}),makeQuery(id+"Fu1y5GcWRBi5nUe_1.opExtrude","SWEPT_FACE",FACE,{"disambiguationData":[OSD([sQuery(id+"F5.wireOp",EDGE,"E57.15.0.7")])]}),makeQuery(id+"Fu1y5GcWRBi5nUe_1.opExtrude","SWEPT_FACE",FACE,{"disambiguationData":[OSD([sQuery(id+"F5.wireOp",EDGE,"E57.16.0.6")])]}),makeQuery(id+"Fu1y5GcWRBi5nUe_1.opExtrude","SWEPT_FACE",FACE,{"disambiguationData":[OSD([sQuery(id+"F5.wireOp",EDGE,"E57.16.0.7")])]}),makeQuery(id+"Fu1y5GcWRBi5nUe_1.opExtrude","SWEPT_FACE",FACE,{"disambiguationData":[OSD([sQuery(id+"F5.wireOp",EDGE,"E57.17.0.6")])]}),makeQuery(id+"Fu1y5GcWRBi5nUe_1.opExtrude","SWEPT_FACE",FACE,{"disambiguationData":[OSD([sQuery(id+"F5.wireOp",EDGE,"E57.17.0.7")])]}),makeQuery(id+"Fu1y5GcWRBi5nUe_1.opExtrude","SWEPT_FACE",FACE,{"disambiguationData":[OSD([sQuery(id+"F5.wireOp",EDGE,"E57.18.0.6")])]}),makeQuery(id+"Fu1y5GcWRBi5nUe_1.opExtrude","SWEPT_FACE",FACE,{"disambiguationData":[OSD([sQuery(id+"F5.wireOp",EDGE,"E57.18.0.7")])]}),makeQuery(id+"Fu1y5GcWRBi5nUe_1.opExtrude","SWEPT_FACE",FACE,{"disambiguationData":[OSD([sQuery(id+"F5.wireOp",EDGE,"E57.19.0.6")])]}),makeQuery(id+"Fu1y5GcWRBi5nUe_1.opExtrude","SWEPT_FACE",FACE,{"disambiguationData":[OSD([sQuery(id+"F5.wireOp",EDGE,"E57.19.0.7")])]}),makeQuery(id+"Fu1y5GcWRBi5nUe_1.opExtrude","SWEPT_FACE",FACE,{"disambiguationData":[OSD([sQuery(id+"F5.wireOp",EDGE,"E57.20.0.6")])]}),makeQuery(id+"Fu1y5GcWRBi5nUe_1.opExtrude","SWEPT_FACE",FACE,{"disambiguationData":[OSD([sQuery(id+"F5.wireOp",EDGE,"E57.20.0.7")])]}),makeQuery(id+"Fu1y5GcWRBi5nUe_1.opExtrude","SWEPT_FACE",FACE,{"disambiguationData":[OSD([sQuery(id+"F5.wireOp",EDGE,"E57.21.0.6")])]}),makeQuery(id+"Fu1y5GcWRBi5nUe_1.opExtrude","SWEPT_FACE",FACE,{"disambiguationData":[OSD([sQuery(id+"F5.wireOp",EDGE,"E57.21.0.7")])]}),makeQuery(id+"Fu1y5GcWRBi5nUe_1.opExtrude","SWEPT_FACE",FACE,{"disambiguationData":[OSD([sQuery(id+"F5.wireOp",EDGE,"E57.22.0.6")])]}),makeQuery(id+"Fu1y5GcWRBi5nUe_1.opExtrude","SWEPT_FACE",FACE,{"disambiguationData":[OSD([sQuery(id+"F5.wireOp",EDGE,"E57.22.0.7")])]}),makeQuery(id+"Fu1y5GcWRBi5nUe_1.opExtrude","SWEPT_FACE",FACE,{"disambiguationData":[OSD([sQuery(id+"F5.wireOp",EDGE,"E57.23.0.6")])]}),makeQuery(id+"Fu1y5GcWRBi5nUe_1.opExtrude","SWEPT_FACE",FACE,{"disambiguationData":[OSD([sQuery(id+"F5.wireOp",EDGE,"E57.23.0.7")])]}),makeQuery(id+"Fu1y5GcWRBi5nUe_1.opExtrude","SWEPT_FACE",FACE,{"disambiguationData":[OSD([sQuery(id+"F5.wireOp",EDGE,"E57.24.0.6")])]}),makeQuery(id+"Fu1y5GcWRBi5nUe_1.opExtrude","SWEPT_FACE",FACE,{"disambiguationData":[OSD([sQuery(id+"F5.wireOp",EDGE,"E57.24.0.7")])]})]});
            var sketch = newSketch(context, id + "F6", { "sketchPlane" : qUnion([Q0])});
            skLineSegment(sketch, "E58", {"start": v(7.62, 19.05) * mm, "end": v(7.62, 22) * mm});
            skLineSegment(sketch, "E59", {"start": v(7.94, 23.98) * mm, "end": v(9.52, 28.77) * mm});
            skLineSegment(sketch, "E60", {"start": v(10.12, 29.21) * mm, "end": v(11.43, 29.2) * mm});
            skLineSegment(sketch, "E61", {"start": v(11.43, 29.2) * mm, "end": v(11.43, 14.72) * mm, "construction": true});
            skLineSegment(sketch, "E62", {"start": v(7.62, 19.05) * mm, "end": v(11.43, 19.05) * mm, "construction": true});
            skPoint(sketch, "E63.visualSharp", {"position": v(9.66, 29.21) * mm});
            skArc(sketch, "E63.filletArc", {"start": v(10.12, 29.21) * mm, "mid": v(9.75, 29.09) * mm, "end": v(9.52, 28.77) * mm});
            skPoint(sketch, "E64.visualSharp", {"position": v(7.62, 23.01) * mm});
            skArc(sketch, "E64.filletArc", {"start": v(7.94, 23.98) * mm, "mid": v(7.7, 23) * mm, "end": v(7.62, 22) * mm});
            skLineSegment(sketch, "E65.MirrorCS", {"start": v(12.74, 29.21) * mm, "end": v(11.43, 29.2) * mm});
            skArc(sketch, "E66.MirrorCS", {"start": v(12.74, 29.21) * mm, "mid": v(13.1, 29.09) * mm, "end": v(13.34, 28.77) * mm});
            skLineSegment(sketch, "E67.MirrorCS", {"start": v(14.92, 23.98) * mm, "end": v(13.34, 28.77) * mm});
            skArc(sketch, "E68.MirrorCS", {"start": v(14.92, 23.98) * mm, "mid": v(15.16, 23) * mm, "end": v(15.24, 22) * mm});
            skLineSegment(sketch, "E69.MirrorCS", {"start": v(15.24, 19.05) * mm, "end": v(15.24, 22) * mm});
            skLineSegment(sketch, "E70", {"start": v(15.24, 19.05) * mm, "end": v(7.62, 19.05) * mm});
            skArc(sketch, "E71.1.0.0", {"start": v(27.98, 29.21) * mm, "mid": v(28.35, 29.09) * mm, "end": v(28.58, 28.77) * mm});
            skLineSegment(sketch, "E71.1.0.1", {"start": v(30.16, 23.98) * mm, "end": v(28.58, 28.77) * mm});
            skArc(sketch, "E71.1.0.2", {"start": v(30.16, 23.98) * mm, "mid": v(30.4, 23) * mm, "end": v(30.48, 22) * mm});
            skLineSegment(sketch, "E71.1.0.3", {"start": v(30.48, 19.05) * mm, "end": v(30.48, 22) * mm});
            skLineSegment(sketch, "E71.1.0.4", {"start": v(30.48, 19.05) * mm, "end": v(22.86, 19.05) * mm});
            skLineSegment(sketch, "E71.1.0.5", {"start": v(27.98, 29.21) * mm, "end": v(26.67, 29.21) * mm});
            skLineSegment(sketch, "E71.1.0.6", {"start": v(25.36, 29.2) * mm, "end": v(26.67, 29.2) * mm});
            skArc(sketch, "E71.1.0.7", {"start": v(25.36, 29.21) * mm, "mid": v(25, 29.09) * mm, "end": v(24.76, 28.77) * mm});
            skLineSegment(sketch, "E71.1.0.8", {"start": v(23.18, 23.98) * mm, "end": v(24.76, 28.77) * mm});
            skArc(sketch, "E71.1.0.9", {"start": v(23.18, 23.98) * mm, "mid": v(22.94, 23) * mm, "end": v(22.86, 22) * mm});
            skLineSegment(sketch, "E71.1.0.10", {"start": v(22.86, 19.05) * mm, "end": v(22.86, 22) * mm});
            skArc(sketch, "E71.2.0.0", {"start": v(43.22, 29.21) * mm, "mid": v(43.59, 29.09) * mm, "end": v(43.82, 28.77) * mm});
            skLineSegment(sketch, "E71.2.0.1", {"start": v(45.4, 23.98) * mm, "end": v(43.82, 28.77) * mm});
            skArc(sketch, "E71.2.0.2", {"start": v(45.4, 23.98) * mm, "mid": v(45.64, 23) * mm, "end": v(45.72, 22) * mm});
            skLineSegment(sketch, "E71.2.0.3", {"start": v(45.72, 19.05) * mm, "end": v(45.72, 22) * mm});
            skLineSegment(sketch, "E71.2.0.4", {"start": v(45.72, 19.05) * mm, "end": v(38.1, 19.05) * mm});
            skLineSegment(sketch, "E71.2.0.5", {"start": v(43.22, 29.21) * mm, "end": v(41.91, 29.21) * mm});
            skLineSegment(sketch, "E71.2.0.6", {"start": v(40.6, 29.2) * mm, "end": v(41.91, 29.2) * mm});
            skArc(sketch, "E71.2.0.7", {"start": v(40.6, 29.21) * mm, "mid": v(40.23, 29.09) * mm, "end": v(40, 28.77) * mm});
            skLineSegment(sketch, "E71.2.0.8", {"start": v(38.42, 23.98) * mm, "end": v(40, 28.77) * mm});
            skArc(sketch, "E71.2.0.9", {"start": v(38.42, 23.98) * mm, "mid": v(38.18, 23) * mm, "end": v(38.1, 22) * mm});
            skLineSegment(sketch, "E71.2.0.10", {"start": v(38.1, 19.05) * mm, "end": v(38.1, 22) * mm});
            skArc(sketch, "E71.3.0.0", {"start": v(58.46, 29.21) * mm, "mid": v(58.83, 29.09) * mm, "end": v(59.06, 28.77) * mm});
            skLineSegment(sketch, "E71.3.0.1", {"start": v(60.64, 23.98) * mm, "end": v(59.06, 28.77) * mm});
            skArc(sketch, "E71.3.0.2", {"start": v(60.64, 23.98) * mm, "mid": v(60.88, 23) * mm, "end": v(60.96, 22) * mm});
            skLineSegment(sketch, "E71.3.0.3", {"start": v(60.96, 19.05) * mm, "end": v(60.96, 22) * mm});
            skLineSegment(sketch, "E71.3.0.4", {"start": v(60.96, 19.05) * mm, "end": v(53.34, 19.05) * mm});
            skLineSegment(sketch, "E71.3.0.5", {"start": v(58.46, 29.21) * mm, "end": v(57.15, 29.21) * mm});
            skLineSegment(sketch, "E71.3.0.6", {"start": v(55.84, 29.2) * mm, "end": v(57.15, 29.2) * mm});
            skArc(sketch, "E71.3.0.7", {"start": v(55.84, 29.21) * mm, "mid": v(55.47, 29.09) * mm, "end": v(55.24, 28.77) * mm});
            skLineSegment(sketch, "E71.3.0.8", {"start": v(53.66, 23.98) * mm, "end": v(55.24, 28.77) * mm});
            skArc(sketch, "E71.3.0.9", {"start": v(53.66, 23.98) * mm, "mid": v(53.42, 23) * mm, "end": v(53.34, 22) * mm});
            skLineSegment(sketch, "E71.3.0.10", {"start": v(53.34, 19.05) * mm, "end": v(53.34, 22) * mm});
            skArc(sketch, "E71.4.0.0", {"start": v(73.7, 29.21) * mm, "mid": v(74.07, 29.09) * mm, "end": v(74.3, 28.77) * mm});
            skLineSegment(sketch, "E71.4.0.1", {"start": v(75.88, 23.98) * mm, "end": v(74.3, 28.77) * mm});
            skArc(sketch, "E71.4.0.2", {"start": v(75.88, 23.98) * mm, "mid": v(76.12, 23) * mm, "end": v(76.2, 22) * mm});
            skLineSegment(sketch, "E71.4.0.3", {"start": v(76.2, 19.05) * mm, "end": v(76.2, 22) * mm});
            skLineSegment(sketch, "E71.4.0.4", {"start": v(76.2, 19.05) * mm, "end": v(68.58, 19.05) * mm});
            skLineSegment(sketch, "E71.4.0.5", {"start": v(73.7, 29.21) * mm, "end": v(72.4, 29.21) * mm});
            skLineSegment(sketch, "E71.4.0.6", {"start": v(71.08, 29.2) * mm, "end": v(72.4, 29.2) * mm});
            skArc(sketch, "E71.4.0.7", {"start": v(71.08, 29.21) * mm, "mid": v(70.71, 29.09) * mm, "end": v(70.48, 28.77) * mm});
            skLineSegment(sketch, "E71.4.0.8", {"start": v(68.9, 23.98) * mm, "end": v(70.48, 28.77) * mm});
            skArc(sketch, "E71.4.0.9", {"start": v(68.9, 23.98) * mm, "mid": v(68.66, 23) * mm, "end": v(68.58, 22) * mm});
            skLineSegment(sketch, "E71.4.0.10", {"start": v(68.58, 19.05) * mm, "end": v(68.58, 22) * mm});
            skArc(sketch, "E71.5.0.0", {"start": v(88.94, 29.21) * mm, "mid": v(89.3, 29.09) * mm, "end": v(89.54, 28.77) * mm});
            skLineSegment(sketch, "E71.5.0.1", {"start": v(91.12, 23.98) * mm, "end": v(89.54, 28.77) * mm});
            skArc(sketch, "E71.5.0.2", {"start": v(91.12, 23.98) * mm, "mid": v(91.36, 23) * mm, "end": v(91.44, 22) * mm});
            skLineSegment(sketch, "E71.5.0.3", {"start": v(91.44, 19.05) * mm, "end": v(91.44, 22) * mm});
            skLineSegment(sketch, "E71.5.0.4", {"start": v(91.44, 19.05) * mm, "end": v(83.82, 19.05) * mm});
            skLineSegment(sketch, "E71.5.0.5", {"start": v(88.94, 29.21) * mm, "end": v(87.63, 29.21) * mm});
            skLineSegment(sketch, "E71.5.0.6", {"start": v(86.32, 29.2) * mm, "end": v(87.63, 29.2) * mm});
            skArc(sketch, "E71.5.0.7", {"start": v(86.32, 29.21) * mm, "mid": v(85.95, 29.09) * mm, "end": v(85.72, 28.77) * mm});
            skLineSegment(sketch, "E71.5.0.8", {"start": v(84.14, 23.98) * mm, "end": v(85.72, 28.77) * mm});
            skArc(sketch, "E71.5.0.9", {"start": v(84.14, 23.98) * mm, "mid": v(83.9, 23) * mm, "end": v(83.82, 22) * mm});
            skLineSegment(sketch, "E71.5.0.10", {"start": v(83.82, 19.05) * mm, "end": v(83.82, 22) * mm});
            skArc(sketch, "E71.6.0.0", {"start": v(104.18, 29.21) * mm, "mid": v(104.55, 29.09) * mm, "end": v(104.78, 28.77) * mm});
            skLineSegment(sketch, "E71.6.0.1", {"start": v(106.36, 23.98) * mm, "end": v(104.78, 28.77) * mm});
            skArc(sketch, "E71.6.0.2", {"start": v(106.36, 23.98) * mm, "mid": v(106.6, 23) * mm, "end": v(106.68, 22) * mm});
            skLineSegment(sketch, "E71.6.0.3", {"start": v(106.68, 19.05) * mm, "end": v(106.68, 22) * mm});
            skLineSegment(sketch, "E71.6.0.4", {"start": v(106.68, 19.05) * mm, "end": v(99.06, 19.05) * mm});
            skLineSegment(sketch, "E71.6.0.5", {"start": v(104.18, 29.21) * mm, "end": v(102.87, 29.21) * mm});
            skLineSegment(sketch, "E71.6.0.6", {"start": v(101.56, 29.2) * mm, "end": v(102.87, 29.2) * mm});
            skArc(sketch, "E71.6.0.7", {"start": v(101.56, 29.21) * mm, "mid": v(101.2, 29.09) * mm, "end": v(100.96, 28.77) * mm});
            skLineSegment(sketch, "E71.6.0.8", {"start": v(99.38, 23.98) * mm, "end": v(100.96, 28.77) * mm});
            skArc(sketch, "E71.6.0.9", {"start": v(99.38, 23.98) * mm, "mid": v(99.14, 23) * mm, "end": v(99.06, 22) * mm});
            skLineSegment(sketch, "E71.6.0.10", {"start": v(99.06, 19.05) * mm, "end": v(99.06, 22) * mm});
            skArc(sketch, "E71.7.0.0", {"start": v(119.42, 29.21) * mm, "mid": v(119.79, 29.09) * mm, "end": v(120.02, 28.77) * mm});
            skLineSegment(sketch, "E71.7.0.1", {"start": v(121.6, 23.98) * mm, "end": v(120.02, 28.77) * mm});
            skArc(sketch, "E71.7.0.2", {"start": v(121.6, 23.98) * mm, "mid": v(121.84, 23) * mm, "end": v(121.92, 22) * mm});
            skLineSegment(sketch, "E71.7.0.3", {"start": v(121.92, 19.05) * mm, "end": v(121.92, 22) * mm});
            skLineSegment(sketch, "E71.7.0.4", {"start": v(121.92, 19.05) * mm, "end": v(114.3, 19.05) * mm});
            skLineSegment(sketch, "E71.7.0.5", {"start": v(119.42, 29.21) * mm, "end": v(118.11, 29.21) * mm});
            skLineSegment(sketch, "E71.7.0.6", {"start": v(116.8, 29.2) * mm, "end": v(118.11, 29.2) * mm});
            skArc(sketch, "E71.7.0.7", {"start": v(116.8, 29.21) * mm, "mid": v(116.43, 29.09) * mm, "end": v(116.2, 28.77) * mm});
            skLineSegment(sketch, "E71.7.0.8", {"start": v(114.62, 23.98) * mm, "end": v(116.2, 28.77) * mm});
            skArc(sketch, "E71.7.0.9", {"start": v(114.62, 23.98) * mm, "mid": v(114.38, 23) * mm, "end": v(114.3, 22) * mm});
            skLineSegment(sketch, "E71.7.0.10", {"start": v(114.3, 19.05) * mm, "end": v(114.3, 22) * mm});
            skArc(sketch, "E71.8.0.0", {"start": v(134.66, 29.21) * mm, "mid": v(135.03, 29.09) * mm, "end": v(135.26, 28.77) * mm});
            skLineSegment(sketch, "E71.8.0.1", {"start": v(136.84, 23.98) * mm, "end": v(135.26, 28.77) * mm});
            skArc(sketch, "E71.8.0.2", {"start": v(136.84, 23.98) * mm, "mid": v(137.08, 23) * mm, "end": v(137.16, 22) * mm});
            skLineSegment(sketch, "E71.8.0.3", {"start": v(137.16, 19.05) * mm, "end": v(137.16, 22) * mm});
            skLineSegment(sketch, "E71.8.0.4", {"start": v(137.16, 19.05) * mm, "end": v(129.54, 19.05) * mm});
            skLineSegment(sketch, "E71.8.0.5", {"start": v(134.66, 29.21) * mm, "end": v(133.35, 29.21) * mm});
            skLineSegment(sketch, "E71.8.0.6", {"start": v(132.04, 29.2) * mm, "end": v(133.35, 29.2) * mm});
            skArc(sketch, "E71.8.0.7", {"start": v(132.04, 29.21) * mm, "mid": v(131.67, 29.09) * mm, "end": v(131.44, 28.77) * mm});
            skLineSegment(sketch, "E71.8.0.8", {"start": v(129.86, 23.98) * mm, "end": v(131.44, 28.77) * mm});
            skArc(sketch, "E71.8.0.9", {"start": v(129.86, 23.98) * mm, "mid": v(129.62, 23) * mm, "end": v(129.54, 22) * mm});
            skLineSegment(sketch, "E71.8.0.10", {"start": v(129.54, 19.05) * mm, "end": v(129.54, 22) * mm});
            skArc(sketch, "E71.9.0.0", {"start": v(149.9, 29.21) * mm, "mid": v(150.27, 29.09) * mm, "end": v(150.5, 28.77) * mm});
            skLineSegment(sketch, "E71.9.0.1", {"start": v(152.08, 23.98) * mm, "end": v(150.5, 28.77) * mm});
            skArc(sketch, "E71.9.0.2", {"start": v(152.08, 23.98) * mm, "mid": v(152.32, 23) * mm, "end": v(152.4, 22) * mm});
            skLineSegment(sketch, "E71.9.0.3", {"start": v(152.4, 19.05) * mm, "end": v(152.4, 22) * mm});
            skLineSegment(sketch, "E71.9.0.4", {"start": v(152.4, 19.05) * mm, "end": v(144.78, 19.05) * mm});
            skLineSegment(sketch, "E71.9.0.5", {"start": v(149.9, 29.21) * mm, "end": v(148.6, 29.21) * mm});
            skLineSegment(sketch, "E71.9.0.6", {"start": v(147.28, 29.2) * mm, "end": v(148.6, 29.2) * mm});
            skArc(sketch, "E71.9.0.7", {"start": v(147.28, 29.21) * mm, "mid": v(146.91, 29.09) * mm, "end": v(146.68, 28.77) * mm});
            skLineSegment(sketch, "E71.9.0.8", {"start": v(145.1, 23.98) * mm, "end": v(146.68, 28.77) * mm});
            skArc(sketch, "E71.9.0.9", {"start": v(145.1, 23.98) * mm, "mid": v(144.86, 23) * mm, "end": v(144.78, 22) * mm});
            skLineSegment(sketch, "E71.9.0.10", {"start": v(144.78, 19.05) * mm, "end": v(144.78, 22) * mm});
            skArc(sketch, "E71.10.0.0", {"start": v(165.14, 29.21) * mm, "mid": v(165.5, 29.09) * mm, "end": v(165.74, 28.77) * mm});
            skLineSegment(sketch, "E71.10.0.1", {"start": v(167.32, 23.98) * mm, "end": v(165.74, 28.77) * mm});
            skArc(sketch, "E71.10.0.2", {"start": v(167.32, 23.98) * mm, "mid": v(167.56, 23) * mm, "end": v(167.64, 22) * mm});
            skLineSegment(sketch, "E71.10.0.3", {"start": v(167.64, 19.05) * mm, "end": v(167.64, 22) * mm});
            skLineSegment(sketch, "E71.10.0.4", {"start": v(167.64, 19.05) * mm, "end": v(160.02, 19.05) * mm});
            skLineSegment(sketch, "E71.10.0.5", {"start": v(165.14, 29.21) * mm, "end": v(163.83, 29.21) * mm});
            skLineSegment(sketch, "E71.10.0.6", {"start": v(162.52, 29.2) * mm, "end": v(163.83, 29.2) * mm});
            skArc(sketch, "E71.10.0.7", {"start": v(162.52, 29.21) * mm, "mid": v(162.15, 29.09) * mm, "end": v(161.92, 28.77) * mm});
            skLineSegment(sketch, "E71.10.0.8", {"start": v(160.34, 23.98) * mm, "end": v(161.92, 28.77) * mm});
            skArc(sketch, "E71.10.0.9", {"start": v(160.34, 23.98) * mm, "mid": v(160.1, 23) * mm, "end": v(160.02, 22) * mm});
            skLineSegment(sketch, "E71.10.0.10", {"start": v(160.02, 19.05) * mm, "end": v(160.02, 22) * mm});
            skArc(sketch, "E71.11.0.0", {"start": v(180.38, 29.21) * mm, "mid": v(180.75, 29.09) * mm, "end": v(180.98, 28.77) * mm});
            skLineSegment(sketch, "E71.11.0.1", {"start": v(182.56, 23.98) * mm, "end": v(180.98, 28.77) * mm});
            skArc(sketch, "E71.11.0.2", {"start": v(182.56, 23.98) * mm, "mid": v(182.8, 23) * mm, "end": v(182.88, 22) * mm});
            skLineSegment(sketch, "E71.11.0.3", {"start": v(182.88, 19.05) * mm, "end": v(182.88, 22) * mm});
            skLineSegment(sketch, "E71.11.0.4", {"start": v(182.88, 19.05) * mm, "end": v(175.26, 19.05) * mm});
            skLineSegment(sketch, "E71.11.0.5", {"start": v(180.38, 29.21) * mm, "end": v(179.07, 29.21) * mm});
            skLineSegment(sketch, "E71.11.0.6", {"start": v(177.76, 29.2) * mm, "end": v(179.07, 29.2) * mm});
            skArc(sketch, "E71.11.0.7", {"start": v(177.76, 29.21) * mm, "mid": v(177.4, 29.09) * mm, "end": v(177.16, 28.77) * mm});
            skLineSegment(sketch, "E71.11.0.8", {"start": v(175.58, 23.98) * mm, "end": v(177.16, 28.77) * mm});
            skArc(sketch, "E71.11.0.9", {"start": v(175.58, 23.98) * mm, "mid": v(175.34, 23) * mm, "end": v(175.26, 22) * mm});
            skLineSegment(sketch, "E71.11.0.10", {"start": v(175.26, 19.05) * mm, "end": v(175.26, 22) * mm});
            skArc(sketch, "E71.12.0.0", {"start": v(195.62, 29.21) * mm, "mid": v(195.99, 29.09) * mm, "end": v(196.22, 28.77) * mm});
            skLineSegment(sketch, "E71.12.0.1", {"start": v(197.8, 23.98) * mm, "end": v(196.22, 28.77) * mm});
            skArc(sketch, "E71.12.0.2", {"start": v(197.8, 23.98) * mm, "mid": v(198.04, 23) * mm, "end": v(198.12, 22) * mm});
            skLineSegment(sketch, "E71.12.0.3", {"start": v(198.12, 19.05) * mm, "end": v(198.12, 22) * mm});
            skLineSegment(sketch, "E71.12.0.4", {"start": v(198.12, 19.05) * mm, "end": v(190.5, 19.05) * mm});
            skLineSegment(sketch, "E71.12.0.5", {"start": v(195.62, 29.21) * mm, "end": v(194.31, 29.21) * mm});
            skLineSegment(sketch, "E71.12.0.6", {"start": v(193, 29.2) * mm, "end": v(194.31, 29.2) * mm});
            skArc(sketch, "E71.12.0.7", {"start": v(193, 29.21) * mm, "mid": v(192.63, 29.09) * mm, "end": v(192.4, 28.77) * mm});
            skLineSegment(sketch, "E71.12.0.8", {"start": v(190.82, 23.98) * mm, "end": v(192.4, 28.77) * mm});
            skArc(sketch, "E71.12.0.9", {"start": v(190.82, 23.98) * mm, "mid": v(190.58, 23) * mm, "end": v(190.5, 22) * mm});
            skLineSegment(sketch, "E71.12.0.10", {"start": v(190.5, 19.05) * mm, "end": v(190.5, 22) * mm});
            skArc(sketch, "E71.13.0.0", {"start": v(210.86, 29.21) * mm, "mid": v(211.23, 29.09) * mm, "end": v(211.46, 28.77) * mm});
            skLineSegment(sketch, "E71.13.0.1", {"start": v(213.04, 23.98) * mm, "end": v(211.46, 28.77) * mm});
            skArc(sketch, "E71.13.0.2", {"start": v(213.04, 23.98) * mm, "mid": v(213.28, 23) * mm, "end": v(213.36, 22) * mm});
            skLineSegment(sketch, "E71.13.0.3", {"start": v(213.36, 19.05) * mm, "end": v(213.36, 22) * mm});
            skLineSegment(sketch, "E71.13.0.4", {"start": v(213.36, 19.05) * mm, "end": v(205.74, 19.05) * mm});
            skLineSegment(sketch, "E71.13.0.5", {"start": v(210.86, 29.21) * mm, "end": v(209.55, 29.21) * mm});
            skLineSegment(sketch, "E71.13.0.6", {"start": v(208.24, 29.2) * mm, "end": v(209.55, 29.2) * mm});
            skArc(sketch, "E71.13.0.7", {"start": v(208.24, 29.21) * mm, "mid": v(207.87, 29.09) * mm, "end": v(207.64, 28.77) * mm});
            skLineSegment(sketch, "E71.13.0.8", {"start": v(206.06, 23.98) * mm, "end": v(207.64, 28.77) * mm});
            skArc(sketch, "E71.13.0.9", {"start": v(206.06, 23.98) * mm, "mid": v(205.82, 23) * mm, "end": v(205.74, 22) * mm});
            skLineSegment(sketch, "E71.13.0.10", {"start": v(205.74, 19.05) * mm, "end": v(205.74, 22) * mm});
            skArc(sketch, "E71.14.0.0", {"start": v(226.1, 29.21) * mm, "mid": v(226.47, 29.09) * mm, "end": v(226.7, 28.77) * mm});
            skLineSegment(sketch, "E71.14.0.1", {"start": v(228.28, 23.98) * mm, "end": v(226.7, 28.77) * mm});
            skArc(sketch, "E71.14.0.2", {"start": v(228.28, 23.98) * mm, "mid": v(228.52, 23) * mm, "end": v(228.6, 22) * mm});
            skLineSegment(sketch, "E71.14.0.3", {"start": v(228.6, 19.05) * mm, "end": v(228.6, 22) * mm});
            skLineSegment(sketch, "E71.14.0.4", {"start": v(228.6, 19.05) * mm, "end": v(220.98, 19.05) * mm});
            skLineSegment(sketch, "E71.14.0.5", {"start": v(226.1, 29.21) * mm, "end": v(224.8, 29.21) * mm});
            skLineSegment(sketch, "E71.14.0.6", {"start": v(223.48, 29.2) * mm, "end": v(224.8, 29.2) * mm});
            skArc(sketch, "E71.14.0.7", {"start": v(223.48, 29.21) * mm, "mid": v(223.11, 29.09) * mm, "end": v(222.88, 28.77) * mm});
            skLineSegment(sketch, "E71.14.0.8", {"start": v(221.3, 23.98) * mm, "end": v(222.88, 28.77) * mm});
            skArc(sketch, "E71.14.0.9", {"start": v(221.3, 23.98) * mm, "mid": v(221.06, 23) * mm, "end": v(220.98, 22) * mm});
            skLineSegment(sketch, "E71.14.0.10", {"start": v(220.98, 19.05) * mm, "end": v(220.98, 22) * mm});
            skArc(sketch, "E71.15.0.0", {"start": v(241.34, 29.21) * mm, "mid": v(241.7, 29.09) * mm, "end": v(241.94, 28.77) * mm});
            skLineSegment(sketch, "E71.15.0.1", {"start": v(243.52, 23.98) * mm, "end": v(241.94, 28.77) * mm});
            skArc(sketch, "E71.15.0.2", {"start": v(243.52, 23.98) * mm, "mid": v(243.76, 23) * mm, "end": v(243.84, 22) * mm});
            skLineSegment(sketch, "E71.15.0.3", {"start": v(243.84, 19.05) * mm, "end": v(243.84, 22) * mm});
            skLineSegment(sketch, "E71.15.0.4", {"start": v(243.84, 19.05) * mm, "end": v(236.22, 19.05) * mm});
            skLineSegment(sketch, "E71.15.0.5", {"start": v(241.34, 29.21) * mm, "end": v(240.03, 29.21) * mm});
            skLineSegment(sketch, "E71.15.0.6", {"start": v(238.72, 29.2) * mm, "end": v(240.03, 29.2) * mm});
            skArc(sketch, "E71.15.0.7", {"start": v(238.72, 29.21) * mm, "mid": v(238.35, 29.09) * mm, "end": v(238.12, 28.77) * mm});
            skLineSegment(sketch, "E71.15.0.8", {"start": v(236.54, 23.98) * mm, "end": v(238.12, 28.77) * mm});
            skArc(sketch, "E71.15.0.9", {"start": v(236.54, 23.98) * mm, "mid": v(236.3, 23) * mm, "end": v(236.22, 22) * mm});
            skLineSegment(sketch, "E71.15.0.10", {"start": v(236.22, 19.05) * mm, "end": v(236.22, 22) * mm});
            skArc(sketch, "E71.16.0.0", {"start": v(256.58, 29.21) * mm, "mid": v(256.95, 29.09) * mm, "end": v(257.18, 28.77) * mm});
            skLineSegment(sketch, "E71.16.0.1", {"start": v(258.76, 23.98) * mm, "end": v(257.18, 28.77) * mm});
            skArc(sketch, "E71.16.0.2", {"start": v(258.76, 23.98) * mm, "mid": v(259, 23) * mm, "end": v(259.08, 22) * mm});
            skLineSegment(sketch, "E71.16.0.3", {"start": v(259.08, 19.05) * mm, "end": v(259.08, 22) * mm});
            skLineSegment(sketch, "E71.16.0.4", {"start": v(259.08, 19.05) * mm, "end": v(251.46, 19.05) * mm});
            skLineSegment(sketch, "E71.16.0.5", {"start": v(256.58, 29.21) * mm, "end": v(255.27, 29.21) * mm});
            skLineSegment(sketch, "E71.16.0.6", {"start": v(253.96, 29.2) * mm, "end": v(255.27, 29.2) * mm});
            skArc(sketch, "E71.16.0.7", {"start": v(253.96, 29.21) * mm, "mid": v(253.6, 29.09) * mm, "end": v(253.36, 28.77) * mm});
            skLineSegment(sketch, "E71.16.0.8", {"start": v(251.78, 23.98) * mm, "end": v(253.36, 28.77) * mm});
            skArc(sketch, "E71.16.0.9", {"start": v(251.78, 23.98) * mm, "mid": v(251.54, 23) * mm, "end": v(251.46, 22) * mm});
            skLineSegment(sketch, "E71.16.0.10", {"start": v(251.46, 19.05) * mm, "end": v(251.46, 22) * mm});
            skArc(sketch, "E71.17.0.0", {"start": v(271.82, 29.21) * mm, "mid": v(272.19, 29.09) * mm, "end": v(272.42, 28.77) * mm});
            skLineSegment(sketch, "E71.17.0.1", {"start": v(274, 23.98) * mm, "end": v(272.42, 28.77) * mm});
            skArc(sketch, "E71.17.0.2", {"start": v(274, 23.98) * mm, "mid": v(274.24, 23) * mm, "end": v(274.32, 22) * mm});
            skLineSegment(sketch, "E71.17.0.3", {"start": v(274.32, 19.05) * mm, "end": v(274.32, 22) * mm});
            skLineSegment(sketch, "E71.17.0.4", {"start": v(274.32, 19.05) * mm, "end": v(266.7, 19.05) * mm});
            skLineSegment(sketch, "E71.17.0.5", {"start": v(271.82, 29.21) * mm, "end": v(270.51, 29.21) * mm});
            skLineSegment(sketch, "E71.17.0.6", {"start": v(269.2, 29.2) * mm, "end": v(270.51, 29.2) * mm});
            skArc(sketch, "E71.17.0.7", {"start": v(269.2, 29.21) * mm, "mid": v(268.83, 29.09) * mm, "end": v(268.6, 28.77) * mm});
            skLineSegment(sketch, "E71.17.0.8", {"start": v(267.02, 23.98) * mm, "end": v(268.6, 28.77) * mm});
            skArc(sketch, "E71.17.0.9", {"start": v(267.02, 23.98) * mm, "mid": v(266.78, 23) * mm, "end": v(266.7, 22) * mm});
            skLineSegment(sketch, "E71.17.0.10", {"start": v(266.7, 19.05) * mm, "end": v(266.7, 22) * mm});
            skArc(sketch, "E71.18.0.0", {"start": v(287.06, 29.21) * mm, "mid": v(287.43, 29.09) * mm, "end": v(287.66, 28.77) * mm});
            skLineSegment(sketch, "E71.18.0.1", {"start": v(289.24, 23.98) * mm, "end": v(287.66, 28.77) * mm});
            skArc(sketch, "E71.18.0.2", {"start": v(289.24, 23.98) * mm, "mid": v(289.48, 23) * mm, "end": v(289.56, 22) * mm});
            skLineSegment(sketch, "E71.18.0.3", {"start": v(289.56, 19.05) * mm, "end": v(289.56, 22) * mm});
            skLineSegment(sketch, "E71.18.0.4", {"start": v(289.56, 19.05) * mm, "end": v(281.94, 19.05) * mm});
            skLineSegment(sketch, "E71.18.0.5", {"start": v(287.06, 29.21) * mm, "end": v(285.75, 29.21) * mm});
            skLineSegment(sketch, "E71.18.0.6", {"start": v(284.44, 29.2) * mm, "end": v(285.75, 29.2) * mm});
            skArc(sketch, "E71.18.0.7", {"start": v(284.44, 29.21) * mm, "mid": v(284.07, 29.09) * mm, "end": v(283.84, 28.77) * mm});
            skLineSegment(sketch, "E71.18.0.8", {"start": v(282.26, 23.98) * mm, "end": v(283.84, 28.77) * mm});
            skArc(sketch, "E71.18.0.9", {"start": v(282.26, 23.98) * mm, "mid": v(282.02, 23) * mm, "end": v(281.94, 22) * mm});
            skLineSegment(sketch, "E71.18.0.10", {"start": v(281.94, 19.05) * mm, "end": v(281.94, 22) * mm});
            skArc(sketch, "E71.19.0.0", {"start": v(302.3, 29.21) * mm, "mid": v(302.67, 29.09) * mm, "end": v(302.9, 28.77) * mm});
            skLineSegment(sketch, "E71.19.0.1", {"start": v(304.48, 23.98) * mm, "end": v(302.9, 28.77) * mm});
            skArc(sketch, "E71.19.0.2", {"start": v(304.48, 23.98) * mm, "mid": v(304.72, 23) * mm, "end": v(304.8, 22) * mm});
            skLineSegment(sketch, "E71.19.0.3", {"start": v(304.8, 19.05) * mm, "end": v(304.8, 22) * mm});
            skLineSegment(sketch, "E71.19.0.4", {"start": v(304.8, 19.05) * mm, "end": v(297.18, 19.05) * mm});
            skLineSegment(sketch, "E71.19.0.5", {"start": v(302.3, 29.21) * mm, "end": v(301, 29.21) * mm});
            skLineSegment(sketch, "E71.19.0.6", {"start": v(299.68, 29.2) * mm, "end": v(301, 29.2) * mm});
            skArc(sketch, "E71.19.0.7", {"start": v(299.68, 29.21) * mm, "mid": v(299.31, 29.09) * mm, "end": v(299.08, 28.77) * mm});
            skLineSegment(sketch, "E71.19.0.8", {"start": v(297.5, 23.98) * mm, "end": v(299.08, 28.77) * mm});
            skArc(sketch, "E71.19.0.9", {"start": v(297.5, 23.98) * mm, "mid": v(297.26, 23) * mm, "end": v(297.18, 22) * mm});
            skLineSegment(sketch, "E71.19.0.10", {"start": v(297.18, 19.05) * mm, "end": v(297.18, 22) * mm});
            skArc(sketch, "E71.20.0.0", {"start": v(317.54, 29.21) * mm, "mid": v(317.9, 29.09) * mm, "end": v(318.14, 28.77) * mm});
            skLineSegment(sketch, "E71.20.0.1", {"start": v(319.72, 23.98) * mm, "end": v(318.14, 28.77) * mm});
            skArc(sketch, "E71.20.0.2", {"start": v(319.72, 23.98) * mm, "mid": v(319.96, 23) * mm, "end": v(320.04, 22) * mm});
            skLineSegment(sketch, "E71.20.0.3", {"start": v(320.04, 19.05) * mm, "end": v(320.04, 22) * mm});
            skLineSegment(sketch, "E71.20.0.4", {"start": v(320.04, 19.05) * mm, "end": v(312.42, 19.05) * mm});
            skLineSegment(sketch, "E71.20.0.5", {"start": v(317.54, 29.21) * mm, "end": v(316.23, 29.21) * mm});
            skLineSegment(sketch, "E71.20.0.6", {"start": v(314.92, 29.2) * mm, "end": v(316.23, 29.2) * mm});
            skArc(sketch, "E71.20.0.7", {"start": v(314.92, 29.21) * mm, "mid": v(314.55, 29.09) * mm, "end": v(314.32, 28.77) * mm});
            skLineSegment(sketch, "E71.20.0.8", {"start": v(312.74, 23.98) * mm, "end": v(314.32, 28.77) * mm});
            skArc(sketch, "E71.20.0.9", {"start": v(312.74, 23.98) * mm, "mid": v(312.5, 23) * mm, "end": v(312.42, 22) * mm});
            skLineSegment(sketch, "E71.20.0.10", {"start": v(312.42, 19.05) * mm, "end": v(312.42, 22) * mm});
            skArc(sketch, "E71.21.0.0", {"start": v(332.78, 29.21) * mm, "mid": v(333.15, 29.09) * mm, "end": v(333.38, 28.77) * mm});
            skLineSegment(sketch, "E71.21.0.1", {"start": v(334.96, 23.98) * mm, "end": v(333.38, 28.77) * mm});
            skArc(sketch, "E71.21.0.2", {"start": v(334.96, 23.98) * mm, "mid": v(335.2, 23) * mm, "end": v(335.28, 22) * mm});
            skLineSegment(sketch, "E71.21.0.3", {"start": v(335.28, 19.05) * mm, "end": v(335.28, 22) * mm});
            skLineSegment(sketch, "E71.21.0.4", {"start": v(335.28, 19.05) * mm, "end": v(327.66, 19.05) * mm});
            skLineSegment(sketch, "E71.21.0.5", {"start": v(332.78, 29.21) * mm, "end": v(331.47, 29.21) * mm});
            skLineSegment(sketch, "E71.21.0.6", {"start": v(330.16, 29.2) * mm, "end": v(331.47, 29.2) * mm});
            skArc(sketch, "E71.21.0.7", {"start": v(330.16, 29.21) * mm, "mid": v(329.8, 29.09) * mm, "end": v(329.56, 28.77) * mm});
            skLineSegment(sketch, "E71.21.0.8", {"start": v(327.98, 23.98) * mm, "end": v(329.56, 28.77) * mm});
            skArc(sketch, "E71.21.0.9", {"start": v(327.98, 23.98) * mm, "mid": v(327.74, 23) * mm, "end": v(327.66, 22) * mm});
            skLineSegment(sketch, "E71.21.0.10", {"start": v(327.66, 19.05) * mm, "end": v(327.66, 22) * mm});
            skArc(sketch, "E71.22.0.0", {"start": v(348.02, 29.21) * mm, "mid": v(348.39, 29.09) * mm, "end": v(348.62, 28.77) * mm});
            skLineSegment(sketch, "E71.22.0.1", {"start": v(350.2, 23.98) * mm, "end": v(348.62, 28.77) * mm});
            skArc(sketch, "E71.22.0.2", {"start": v(350.2, 23.98) * mm, "mid": v(350.44, 23) * mm, "end": v(350.52, 22) * mm});
            skLineSegment(sketch, "E71.22.0.3", {"start": v(350.52, 19.05) * mm, "end": v(350.52, 22) * mm});
            skLineSegment(sketch, "E71.22.0.4", {"start": v(350.52, 19.05) * mm, "end": v(342.9, 19.05) * mm});
            skLineSegment(sketch, "E71.22.0.5", {"start": v(348.02, 29.21) * mm, "end": v(346.71, 29.21) * mm});
            skLineSegment(sketch, "E71.22.0.6", {"start": v(345.4, 29.2) * mm, "end": v(346.71, 29.2) * mm});
            skArc(sketch, "E71.22.0.7", {"start": v(345.4, 29.21) * mm, "mid": v(345.03, 29.09) * mm, "end": v(344.8, 28.77) * mm});
            skLineSegment(sketch, "E71.22.0.8", {"start": v(343.22, 23.98) * mm, "end": v(344.8, 28.77) * mm});
            skArc(sketch, "E71.22.0.9", {"start": v(343.22, 23.98) * mm, "mid": v(342.98, 23) * mm, "end": v(342.9, 22) * mm});
            skLineSegment(sketch, "E71.22.0.10", {"start": v(342.9, 19.05) * mm, "end": v(342.9, 22) * mm});
            skArc(sketch, "E71.23.0.0", {"start": v(363.26, 29.21) * mm, "mid": v(363.63, 29.09) * mm, "end": v(363.86, 28.77) * mm});
            skLineSegment(sketch, "E71.23.0.1", {"start": v(365.44, 23.98) * mm, "end": v(363.86, 28.77) * mm});
            skArc(sketch, "E71.23.0.2", {"start": v(365.44, 23.98) * mm, "mid": v(365.68, 23) * mm, "end": v(365.76, 22) * mm});
            skLineSegment(sketch, "E71.23.0.3", {"start": v(365.76, 19.05) * mm, "end": v(365.76, 22) * mm});
            skLineSegment(sketch, "E71.23.0.4", {"start": v(365.76, 19.05) * mm, "end": v(358.14, 19.05) * mm});
            skLineSegment(sketch, "E71.23.0.5", {"start": v(363.26, 29.21) * mm, "end": v(361.95, 29.21) * mm});
            skLineSegment(sketch, "E71.23.0.6", {"start": v(360.64, 29.2) * mm, "end": v(361.95, 29.2) * mm});
            skArc(sketch, "E71.23.0.7", {"start": v(360.64, 29.21) * mm, "mid": v(360.27, 29.09) * mm, "end": v(360.04, 28.77) * mm});
            skLineSegment(sketch, "E71.23.0.8", {"start": v(358.46, 23.98) * mm, "end": v(360.04, 28.77) * mm});
            skArc(sketch, "E71.23.0.9", {"start": v(358.46, 23.98) * mm, "mid": v(358.22, 23) * mm, "end": v(358.14, 22) * mm});
            skLineSegment(sketch, "E71.23.0.10", {"start": v(358.14, 19.05) * mm, "end": v(358.14, 22) * mm});
            skArc(sketch, "E71.24.0.0", {"start": v(378.5, 29.21) * mm, "mid": v(378.87, 29.09) * mm, "end": v(379.1, 28.77) * mm});
            skLineSegment(sketch, "E71.24.0.1", {"start": v(380.68, 23.98) * mm, "end": v(379.1, 28.77) * mm});
            skArc(sketch, "E71.24.0.2", {"start": v(380.68, 23.98) * mm, "mid": v(380.92, 23) * mm, "end": v(381, 22) * mm});
            skLineSegment(sketch, "E71.24.0.3", {"start": v(381, 19.05) * mm, "end": v(381, 22) * mm});
            skLineSegment(sketch, "E71.24.0.4", {"start": v(381, 19.05) * mm, "end": v(373.38, 19.05) * mm});
            skLineSegment(sketch, "E71.24.0.5", {"start": v(378.5, 29.21) * mm, "end": v(377.2, 29.21) * mm});
            skLineSegment(sketch, "E71.24.0.6", {"start": v(375.88, 29.2) * mm, "end": v(377.2, 29.2) * mm});
            skArc(sketch, "E71.24.0.7", {"start": v(375.88, 29.21) * mm, "mid": v(375.51, 29.09) * mm, "end": v(375.28, 28.77) * mm});
            skLineSegment(sketch, "E71.24.0.8", {"start": v(373.7, 23.98) * mm, "end": v(375.28, 28.77) * mm});
            skArc(sketch, "E71.24.0.9", {"start": v(373.7, 23.98) * mm, "mid": v(373.46, 23) * mm, "end": v(373.38, 22) * mm});
            skLineSegment(sketch, "E71.24.0.10", {"start": v(373.38, 19.05) * mm, "end": v(373.38, 22) * mm});
            skArc(sketch, "E71.25.0.0", {"start": v(393.74, 29.21) * mm, "mid": v(394.1, 29.09) * mm, "end": v(394.34, 28.77) * mm});
            skLineSegment(sketch, "E71.25.0.1", {"start": v(395.92, 23.98) * mm, "end": v(394.34, 28.77) * mm});
            skArc(sketch, "E71.25.0.2", {"start": v(395.92, 23.98) * mm, "mid": v(396.16, 23) * mm, "end": v(396.24, 22) * mm});
            skLineSegment(sketch, "E71.25.0.3", {"start": v(396.24, 19.05) * mm, "end": v(396.24, 22) * mm});
            skLineSegment(sketch, "E71.25.0.4", {"start": v(396.24, 19.05) * mm, "end": v(388.62, 19.05) * mm});
            skLineSegment(sketch, "E71.25.0.5", {"start": v(393.74, 29.21) * mm, "end": v(392.43, 29.21) * mm});
            skLineSegment(sketch, "E71.25.0.6", {"start": v(391.12, 29.2) * mm, "end": v(392.43, 29.2) * mm});
            skArc(sketch, "E71.25.0.7", {"start": v(391.12, 29.21) * mm, "mid": v(390.75, 29.09) * mm, "end": v(390.52, 28.77) * mm});
            skLineSegment(sketch, "E71.25.0.8", {"start": v(388.94, 23.98) * mm, "end": v(390.52, 28.77) * mm});
            skArc(sketch, "E71.25.0.9", {"start": v(388.94, 23.98) * mm, "mid": v(388.7, 23) * mm, "end": v(388.62, 22) * mm});
            skLineSegment(sketch, "E71.25.0.10", {"start": v(388.62, 19.05) * mm, "end": v(388.62, 22) * mm});
            skArc(sketch, "E71.26.0.0", {"start": v(408.98, 29.21) * mm, "mid": v(409.35, 29.09) * mm, "end": v(409.58, 28.77) * mm});
            skLineSegment(sketch, "E71.26.0.1", {"start": v(411.16, 23.98) * mm, "end": v(409.58, 28.77) * mm});
            skArc(sketch, "E71.26.0.2", {"start": v(411.16, 23.98) * mm, "mid": v(411.4, 23) * mm, "end": v(411.48, 22) * mm});
            skLineSegment(sketch, "E71.26.0.3", {"start": v(411.48, 19.05) * mm, "end": v(411.48, 22) * mm});
            skLineSegment(sketch, "E71.26.0.4", {"start": v(411.48, 19.05) * mm, "end": v(403.86, 19.05) * mm});
            skLineSegment(sketch, "E71.26.0.5", {"start": v(408.98, 29.21) * mm, "end": v(407.67, 29.21) * mm});
            skLineSegment(sketch, "E71.26.0.6", {"start": v(406.36, 29.2) * mm, "end": v(407.67, 29.2) * mm});
            skArc(sketch, "E71.26.0.7", {"start": v(406.36, 29.21) * mm, "mid": v(406, 29.09) * mm, "end": v(405.76, 28.77) * mm});
            skLineSegment(sketch, "E71.26.0.8", {"start": v(404.18, 23.98) * mm, "end": v(405.76, 28.77) * mm});
            skArc(sketch, "E71.26.0.9", {"start": v(404.18, 23.98) * mm, "mid": v(403.94, 23) * mm, "end": v(403.86, 22) * mm});
            skLineSegment(sketch, "E71.26.0.10", {"start": v(403.86, 19.05) * mm, "end": v(403.86, 22) * mm});
            skArc(sketch, "E71.27.0.0", {"start": v(424.22, 29.21) * mm, "mid": v(424.59, 29.09) * mm, "end": v(424.82, 28.77) * mm});
            skLineSegment(sketch, "E71.27.0.1", {"start": v(426.4, 23.98) * mm, "end": v(424.82, 28.77) * mm});
            skArc(sketch, "E71.27.0.2", {"start": v(426.4, 23.98) * mm, "mid": v(426.64, 23) * mm, "end": v(426.72, 22) * mm});
            skLineSegment(sketch, "E71.27.0.3", {"start": v(426.72, 19.05) * mm, "end": v(426.72, 22) * mm});
            skLineSegment(sketch, "E71.27.0.4", {"start": v(426.72, 19.05) * mm, "end": v(419.1, 19.05) * mm});
            skLineSegment(sketch, "E71.27.0.5", {"start": v(424.22, 29.21) * mm, "end": v(422.91, 29.21) * mm});
            skLineSegment(sketch, "E71.27.0.6", {"start": v(421.6, 29.2) * mm, "end": v(422.91, 29.2) * mm});
            skArc(sketch, "E71.27.0.7", {"start": v(421.6, 29.21) * mm, "mid": v(421.23, 29.09) * mm, "end": v(421, 28.77) * mm});
            skLineSegment(sketch, "E71.27.0.8", {"start": v(419.42, 23.98) * mm, "end": v(421, 28.77) * mm});
            skArc(sketch, "E71.27.0.9", {"start": v(419.42, 23.98) * mm, "mid": v(419.18, 23) * mm, "end": v(419.1, 22) * mm});
            skLineSegment(sketch, "E71.27.0.10", {"start": v(419.1, 19.05) * mm, "end": v(419.1, 22) * mm});
            skArc(sketch, "E71.28.0.0", {"start": v(439.46, 29.21) * mm, "mid": v(439.83, 29.09) * mm, "end": v(440.06, 28.77) * mm});
            skLineSegment(sketch, "E71.28.0.1", {"start": v(441.64, 23.98) * mm, "end": v(440.06, 28.77) * mm});
            skArc(sketch, "E71.28.0.2", {"start": v(441.64, 23.98) * mm, "mid": v(441.88, 23) * mm, "end": v(441.96, 22) * mm});
            skLineSegment(sketch, "E71.28.0.3", {"start": v(441.96, 19.05) * mm, "end": v(441.96, 22) * mm});
            skLineSegment(sketch, "E71.28.0.4", {"start": v(441.96, 19.05) * mm, "end": v(434.34, 19.05) * mm});
            skLineSegment(sketch, "E71.28.0.5", {"start": v(439.46, 29.21) * mm, "end": v(438.15, 29.21) * mm});
            skLineSegment(sketch, "E71.28.0.6", {"start": v(436.84, 29.2) * mm, "end": v(438.15, 29.2) * mm});
            skArc(sketch, "E71.28.0.7", {"start": v(436.84, 29.21) * mm, "mid": v(436.47, 29.09) * mm, "end": v(436.24, 28.77) * mm});
            skLineSegment(sketch, "E71.28.0.8", {"start": v(434.66, 23.98) * mm, "end": v(436.24, 28.77) * mm});
            skArc(sketch, "E71.28.0.9", {"start": v(434.66, 23.98) * mm, "mid": v(434.42, 23) * mm, "end": v(434.34, 22) * mm});
            skLineSegment(sketch, "E71.28.0.10", {"start": v(434.34, 19.05) * mm, "end": v(434.34, 22) * mm});
            skArc(sketch, "E71.29.0.0", {"start": v(454.7, 29.21) * mm, "mid": v(455.07, 29.09) * mm, "end": v(455.3, 28.77) * mm});
            skLineSegment(sketch, "E71.29.0.1", {"start": v(456.88, 23.98) * mm, "end": v(455.3, 28.77) * mm});
            skArc(sketch, "E71.29.0.2", {"start": v(456.88, 23.98) * mm, "mid": v(457.12, 23) * mm, "end": v(457.2, 22) * mm});
            skLineSegment(sketch, "E71.29.0.3", {"start": v(457.2, 19.05) * mm, "end": v(457.2, 22) * mm});
            skLineSegment(sketch, "E71.29.0.4", {"start": v(457.2, 19.05) * mm, "end": v(449.58, 19.05) * mm});
            skLineSegment(sketch, "E71.29.0.5", {"start": v(454.7, 29.21) * mm, "end": v(453.4, 29.21) * mm});
            skLineSegment(sketch, "E71.29.0.6", {"start": v(452.08, 29.2) * mm, "end": v(453.4, 29.2) * mm});
            skArc(sketch, "E71.29.0.7", {"start": v(452.08, 29.21) * mm, "mid": v(451.71, 29.09) * mm, "end": v(451.48, 28.77) * mm});
            skLineSegment(sketch, "E71.29.0.8", {"start": v(449.9, 23.98) * mm, "end": v(451.48, 28.77) * mm});
            skArc(sketch, "E71.29.0.9", {"start": v(449.9, 23.98) * mm, "mid": v(449.66, 23) * mm, "end": v(449.58, 22) * mm});
            skLineSegment(sketch, "E71.29.0.10", {"start": v(449.58, 19.05) * mm, "end": v(449.58, 22) * mm});
            skArc(sketch, "E71.30.0.0", {"start": v(469.94, 29.21) * mm, "mid": v(470.3, 29.09) * mm, "end": v(470.54, 28.77) * mm});
            skLineSegment(sketch, "E71.30.0.1", {"start": v(472.12, 23.98) * mm, "end": v(470.54, 28.77) * mm});
            skArc(sketch, "E71.30.0.2", {"start": v(472.12, 23.98) * mm, "mid": v(472.36, 23) * mm, "end": v(472.44, 22) * mm});
            skLineSegment(sketch, "E71.30.0.3", {"start": v(472.44, 19.05) * mm, "end": v(472.44, 22) * mm});
            skLineSegment(sketch, "E71.30.0.4", {"start": v(472.44, 19.05) * mm, "end": v(464.82, 19.05) * mm});
            skLineSegment(sketch, "E71.30.0.5", {"start": v(469.94, 29.21) * mm, "end": v(468.63, 29.21) * mm});
            skLineSegment(sketch, "E71.30.0.6", {"start": v(467.32, 29.2) * mm, "end": v(468.63, 29.2) * mm});
            skArc(sketch, "E71.30.0.7", {"start": v(467.32, 29.21) * mm, "mid": v(466.95, 29.09) * mm, "end": v(466.72, 28.77) * mm});
            skLineSegment(sketch, "E71.30.0.8", {"start": v(465.14, 23.98) * mm, "end": v(466.72, 28.77) * mm});
            skArc(sketch, "E71.30.0.9", {"start": v(465.14, 23.98) * mm, "mid": v(464.9, 23) * mm, "end": v(464.82, 22) * mm});
            skLineSegment(sketch, "E71.30.0.10", {"start": v(464.82, 19.05) * mm, "end": v(464.82, 22) * mm});
            skArc(sketch, "E71.31.0.0", {"start": v(485.18, 29.21) * mm, "mid": v(485.55, 29.09) * mm, "end": v(485.78, 28.77) * mm});
            skLineSegment(sketch, "E71.31.0.1", {"start": v(487.36, 23.98) * mm, "end": v(485.78, 28.77) * mm});
            skArc(sketch, "E71.31.0.2", {"start": v(487.36, 23.98) * mm, "mid": v(487.6, 23) * mm, "end": v(487.68, 22) * mm});
            skLineSegment(sketch, "E71.31.0.3", {"start": v(487.68, 19.05) * mm, "end": v(487.68, 22) * mm});
            skLineSegment(sketch, "E71.31.0.4", {"start": v(487.68, 19.05) * mm, "end": v(480.06, 19.05) * mm});
            skLineSegment(sketch, "E71.31.0.5", {"start": v(485.18, 29.21) * mm, "end": v(483.87, 29.21) * mm});
            skLineSegment(sketch, "E71.31.0.6", {"start": v(482.56, 29.2) * mm, "end": v(483.87, 29.2) * mm});
            skArc(sketch, "E71.31.0.7", {"start": v(482.56, 29.21) * mm, "mid": v(482.2, 29.09) * mm, "end": v(481.96, 28.77) * mm});
            skLineSegment(sketch, "E71.31.0.8", {"start": v(480.38, 23.98) * mm, "end": v(481.96, 28.77) * mm});
            skArc(sketch, "E71.31.0.9", {"start": v(480.38, 23.98) * mm, "mid": v(480.14, 23) * mm, "end": v(480.06, 22) * mm});
            skLineSegment(sketch, "E71.31.0.10", {"start": v(480.06, 19.05) * mm, "end": v(480.06, 22) * mm});
            skArc(sketch, "E71.32.0.0", {"start": v(500.42, 29.21) * mm, "mid": v(500.79, 29.09) * mm, "end": v(501.02, 28.77) * mm});
            skLineSegment(sketch, "E71.32.0.1", {"start": v(502.6, 23.98) * mm, "end": v(501.02, 28.77) * mm});
            skArc(sketch, "E71.32.0.2", {"start": v(502.6, 23.98) * mm, "mid": v(502.84, 23) * mm, "end": v(502.92, 22) * mm});
            skLineSegment(sketch, "E71.32.0.3", {"start": v(502.92, 19.05) * mm, "end": v(502.92, 22) * mm});
            skLineSegment(sketch, "E71.32.0.4", {"start": v(502.92, 19.05) * mm, "end": v(495.3, 19.05) * mm});
            skLineSegment(sketch, "E71.32.0.5", {"start": v(500.42, 29.21) * mm, "end": v(499.11, 29.21) * mm});
            skLineSegment(sketch, "E71.32.0.6", {"start": v(497.8, 29.2) * mm, "end": v(499.11, 29.2) * mm});
            skArc(sketch, "E71.32.0.7", {"start": v(497.8, 29.21) * mm, "mid": v(497.43, 29.09) * mm, "end": v(497.2, 28.77) * mm});
            skLineSegment(sketch, "E71.32.0.8", {"start": v(495.62, 23.98) * mm, "end": v(497.2, 28.77) * mm});
            skArc(sketch, "E71.32.0.9", {"start": v(495.62, 23.98) * mm, "mid": v(495.38, 23) * mm, "end": v(495.3, 22) * mm});
            skLineSegment(sketch, "E71.32.0.10", {"start": v(495.3, 19.05) * mm, "end": v(495.3, 22) * mm});
            skArc(sketch, "E71.33.0.0", {"start": v(515.66, 29.21) * mm, "mid": v(516.03, 29.09) * mm, "end": v(516.26, 28.77) * mm});
            skLineSegment(sketch, "E71.33.0.1", {"start": v(517.84, 23.98) * mm, "end": v(516.26, 28.77) * mm});
            skArc(sketch, "E71.33.0.2", {"start": v(517.84, 23.98) * mm, "mid": v(518.08, 23) * mm, "end": v(518.16, 22) * mm});
            skLineSegment(sketch, "E71.33.0.3", {"start": v(518.16, 19.05) * mm, "end": v(518.16, 22) * mm});
            skLineSegment(sketch, "E71.33.0.4", {"start": v(518.16, 19.05) * mm, "end": v(510.54, 19.05) * mm});
            skLineSegment(sketch, "E71.33.0.5", {"start": v(515.66, 29.21) * mm, "end": v(514.35, 29.21) * mm});
            skLineSegment(sketch, "E71.33.0.6", {"start": v(513.04, 29.2) * mm, "end": v(514.35, 29.2) * mm});
            skArc(sketch, "E71.33.0.7", {"start": v(513.04, 29.21) * mm, "mid": v(512.67, 29.09) * mm, "end": v(512.44, 28.77) * mm});
            skLineSegment(sketch, "E71.33.0.8", {"start": v(510.86, 23.98) * mm, "end": v(512.44, 28.77) * mm});
            skArc(sketch, "E71.33.0.9", {"start": v(510.86, 23.98) * mm, "mid": v(510.62, 23) * mm, "end": v(510.54, 22) * mm});
            skLineSegment(sketch, "E71.33.0.10", {"start": v(510.54, 19.05) * mm, "end": v(510.54, 22) * mm});
            skArc(sketch, "E71.34.0.0", {"start": v(530.9, 29.21) * mm, "mid": v(531.27, 29.09) * mm, "end": v(531.5, 28.77) * mm});
            skLineSegment(sketch, "E71.34.0.1", {"start": v(533.08, 23.98) * mm, "end": v(531.5, 28.77) * mm});
            skArc(sketch, "E71.34.0.2", {"start": v(533.08, 23.98) * mm, "mid": v(533.32, 23) * mm, "end": v(533.4, 22) * mm});
            skLineSegment(sketch, "E71.34.0.3", {"start": v(533.4, 19.05) * mm, "end": v(533.4, 22) * mm});
            skLineSegment(sketch, "E71.34.0.4", {"start": v(533.4, 19.05) * mm, "end": v(525.78, 19.05) * mm});
            skLineSegment(sketch, "E71.34.0.5", {"start": v(530.9, 29.21) * mm, "end": v(529.6, 29.21) * mm});
            skLineSegment(sketch, "E71.34.0.6", {"start": v(528.28, 29.2) * mm, "end": v(529.6, 29.2) * mm});
            skArc(sketch, "E71.34.0.7", {"start": v(528.28, 29.21) * mm, "mid": v(527.91, 29.09) * mm, "end": v(527.68, 28.77) * mm});
            skLineSegment(sketch, "E71.34.0.8", {"start": v(526.1, 23.98) * mm, "end": v(527.68, 28.77) * mm});
            skArc(sketch, "E71.34.0.9", {"start": v(526.1, 23.98) * mm, "mid": v(525.86, 23) * mm, "end": v(525.78, 22) * mm});
            skLineSegment(sketch, "E71.34.0.10", {"start": v(525.78, 19.05) * mm, "end": v(525.78, 22) * mm});
            skArc(sketch, "E71.35.0.0", {"start": v(546.14, 29.21) * mm, "mid": v(546.5, 29.09) * mm, "end": v(546.74, 28.77) * mm});
            skLineSegment(sketch, "E71.35.0.1", {"start": v(548.32, 23.98) * mm, "end": v(546.74, 28.77) * mm});
            skArc(sketch, "E71.35.0.2", {"start": v(548.32, 23.98) * mm, "mid": v(548.56, 23) * mm, "end": v(548.64, 22) * mm});
            skLineSegment(sketch, "E71.35.0.3", {"start": v(548.64, 19.05) * mm, "end": v(548.64, 22) * mm});
            skLineSegment(sketch, "E71.35.0.4", {"start": v(548.64, 19.05) * mm, "end": v(541.02, 19.05) * mm});
            skLineSegment(sketch, "E71.35.0.5", {"start": v(546.14, 29.21) * mm, "end": v(544.83, 29.21) * mm});
            skLineSegment(sketch, "E71.35.0.6", {"start": v(543.52, 29.2) * mm, "end": v(544.83, 29.2) * mm});
            skArc(sketch, "E71.35.0.7", {"start": v(543.52, 29.21) * mm, "mid": v(543.15, 29.09) * mm, "end": v(542.92, 28.77) * mm});
            skLineSegment(sketch, "E71.35.0.8", {"start": v(541.34, 23.98) * mm, "end": v(542.92, 28.77) * mm});
            skArc(sketch, "E71.35.0.9", {"start": v(541.34, 23.98) * mm, "mid": v(541.1, 23) * mm, "end": v(541.02, 22) * mm});
            skLineSegment(sketch, "E71.35.0.10", {"start": v(541.02, 19.05) * mm, "end": v(541.02, 22) * mm});
            skArc(sketch, "E71.36.0.0", {"start": v(561.38, 29.21) * mm, "mid": v(561.75, 29.09) * mm, "end": v(561.98, 28.77) * mm});
            skLineSegment(sketch, "E71.36.0.1", {"start": v(563.56, 23.98) * mm, "end": v(561.98, 28.77) * mm});
            skArc(sketch, "E71.36.0.2", {"start": v(563.56, 23.98) * mm, "mid": v(563.8, 23) * mm, "end": v(563.88, 22) * mm});
            skLineSegment(sketch, "E71.36.0.3", {"start": v(563.88, 19.05) * mm, "end": v(563.88, 22) * mm});
            skLineSegment(sketch, "E71.36.0.4", {"start": v(563.88, 19.05) * mm, "end": v(556.26, 19.05) * mm});
            skLineSegment(sketch, "E71.36.0.5", {"start": v(561.38, 29.21) * mm, "end": v(560.07, 29.21) * mm});
            skLineSegment(sketch, "E71.36.0.6", {"start": v(558.76, 29.2) * mm, "end": v(560.07, 29.2) * mm});
            skArc(sketch, "E71.36.0.7", {"start": v(558.76, 29.21) * mm, "mid": v(558.4, 29.09) * mm, "end": v(558.16, 28.77) * mm});
            skLineSegment(sketch, "E71.36.0.8", {"start": v(556.58, 23.98) * mm, "end": v(558.16, 28.77) * mm});
            skArc(sketch, "E71.36.0.9", {"start": v(556.58, 23.98) * mm, "mid": v(556.34, 23) * mm, "end": v(556.26, 22) * mm});
            skLineSegment(sketch, "E71.36.0.10", {"start": v(556.26, 19.05) * mm, "end": v(556.26, 22) * mm});
            skArc(sketch, "E71.37.0.0", {"start": v(576.62, 29.21) * mm, "mid": v(576.99, 29.09) * mm, "end": v(577.22, 28.77) * mm});
            skLineSegment(sketch, "E71.37.0.1", {"start": v(578.8, 23.98) * mm, "end": v(577.22, 28.77) * mm});
            skArc(sketch, "E71.37.0.2", {"start": v(578.8, 23.98) * mm, "mid": v(579.04, 23) * mm, "end": v(579.12, 22) * mm});
            skLineSegment(sketch, "E71.37.0.3", {"start": v(579.12, 19.05) * mm, "end": v(579.12, 22) * mm});
            skLineSegment(sketch, "E71.37.0.4", {"start": v(579.12, 19.05) * mm, "end": v(571.5, 19.05) * mm});
            skLineSegment(sketch, "E71.37.0.5", {"start": v(576.62, 29.21) * mm, "end": v(575.31, 29.21) * mm});
            skLineSegment(sketch, "E71.37.0.6", {"start": v(574, 29.2) * mm, "end": v(575.31, 29.2) * mm});
            skArc(sketch, "E71.37.0.7", {"start": v(574, 29.21) * mm, "mid": v(573.63, 29.09) * mm, "end": v(573.4, 28.77) * mm});
            skLineSegment(sketch, "E71.37.0.8", {"start": v(571.82, 23.98) * mm, "end": v(573.4, 28.77) * mm});
            skArc(sketch, "E71.37.0.9", {"start": v(571.82, 23.98) * mm, "mid": v(571.58, 23) * mm, "end": v(571.5, 22) * mm});
            skLineSegment(sketch, "E71.37.0.10", {"start": v(571.5, 19.05) * mm, "end": v(571.5, 22) * mm});
            skArc(sketch, "E71.38.0.0", {"start": v(591.86, 29.21) * mm, "mid": v(592.23, 29.09) * mm, "end": v(592.46, 28.77) * mm});
            skLineSegment(sketch, "E71.38.0.1", {"start": v(594.04, 23.98) * mm, "end": v(592.46, 28.77) * mm});
            skArc(sketch, "E71.38.0.2", {"start": v(594.04, 23.98) * mm, "mid": v(594.28, 23) * mm, "end": v(594.36, 22) * mm});
            skLineSegment(sketch, "E71.38.0.3", {"start": v(594.36, 19.05) * mm, "end": v(594.36, 22) * mm});
            skLineSegment(sketch, "E71.38.0.4", {"start": v(594.36, 19.05) * mm, "end": v(586.74, 19.05) * mm});
            skLineSegment(sketch, "E71.38.0.5", {"start": v(591.86, 29.21) * mm, "end": v(590.55, 29.21) * mm});
            skLineSegment(sketch, "E71.38.0.6", {"start": v(589.24, 29.2) * mm, "end": v(590.55, 29.2) * mm});
            skArc(sketch, "E71.38.0.7", {"start": v(589.24, 29.21) * mm, "mid": v(588.87, 29.09) * mm, "end": v(588.64, 28.77) * mm});
            skLineSegment(sketch, "E71.38.0.8", {"start": v(587.06, 23.98) * mm, "end": v(588.64, 28.77) * mm});
            skArc(sketch, "E71.38.0.9", {"start": v(587.06, 23.98) * mm, "mid": v(586.82, 23) * mm, "end": v(586.74, 22) * mm});
            skLineSegment(sketch, "E71.38.0.10", {"start": v(586.74, 19.05) * mm, "end": v(586.74, 22) * mm});
            skArc(sketch, "E71.39.0.0", {"start": v(607.1, 29.21) * mm, "mid": v(607.47, 29.09) * mm, "end": v(607.7, 28.77) * mm});
            skLineSegment(sketch, "E71.39.0.1", {"start": v(609.28, 23.98) * mm, "end": v(607.7, 28.77) * mm});
            skArc(sketch, "E71.39.0.2", {"start": v(609.28, 23.98) * mm, "mid": v(609.52, 23) * mm, "end": v(609.6, 22) * mm});
            skLineSegment(sketch, "E71.39.0.3", {"start": v(609.6, 19.05) * mm, "end": v(609.6, 22) * mm});
            skLineSegment(sketch, "E71.39.0.4", {"start": v(609.6, 19.05) * mm, "end": v(601.98, 19.05) * mm});
            skLineSegment(sketch, "E71.39.0.5", {"start": v(607.1, 29.21) * mm, "end": v(605.8, 29.21) * mm});
            skLineSegment(sketch, "E71.39.0.6", {"start": v(604.48, 29.2) * mm, "end": v(605.8, 29.2) * mm});
            skArc(sketch, "E71.39.0.7", {"start": v(604.48, 29.21) * mm, "mid": v(604.11, 29.09) * mm, "end": v(603.88, 28.77) * mm});
            skLineSegment(sketch, "E71.39.0.8", {"start": v(602.3, 23.98) * mm, "end": v(603.88, 28.77) * mm});
            skArc(sketch, "E71.39.0.9", {"start": v(602.3, 23.98) * mm, "mid": v(602.06, 23) * mm, "end": v(601.98, 22) * mm});
            skLineSegment(sketch, "E71.39.0.10", {"start": v(601.98, 19.05) * mm, "end": v(601.98, 22) * mm});
            skArc(sketch, "E71.40.0.0", {"start": v(622.34, 29.21) * mm, "mid": v(622.7, 29.09) * mm, "end": v(622.94, 28.77) * mm});
            skLineSegment(sketch, "E71.40.0.1", {"start": v(624.52, 23.98) * mm, "end": v(622.94, 28.77) * mm});
            skArc(sketch, "E71.40.0.2", {"start": v(624.52, 23.98) * mm, "mid": v(624.76, 23) * mm, "end": v(624.84, 22) * mm});
            skLineSegment(sketch, "E71.40.0.3", {"start": v(624.84, 19.05) * mm, "end": v(624.84, 22) * mm});
            skLineSegment(sketch, "E71.40.0.4", {"start": v(624.84, 19.05) * mm, "end": v(617.22, 19.05) * mm});
            skLineSegment(sketch, "E71.40.0.5", {"start": v(622.34, 29.21) * mm, "end": v(621.03, 29.21) * mm});
            skLineSegment(sketch, "E71.40.0.6", {"start": v(619.72, 29.2) * mm, "end": v(621.03, 29.2) * mm});
            skArc(sketch, "E71.40.0.7", {"start": v(619.72, 29.21) * mm, "mid": v(619.35, 29.09) * mm, "end": v(619.12, 28.77) * mm});
            skLineSegment(sketch, "E71.40.0.8", {"start": v(617.54, 23.98) * mm, "end": v(619.12, 28.77) * mm});
            skArc(sketch, "E71.40.0.9", {"start": v(617.54, 23.98) * mm, "mid": v(617.3, 23) * mm, "end": v(617.22, 22) * mm});
            skLineSegment(sketch, "E71.40.0.10", {"start": v(617.22, 19.05) * mm, "end": v(617.22, 22) * mm});
            skArc(sketch, "E71.41.0.0", {"start": v(637.58, 29.21) * mm, "mid": v(637.95, 29.09) * mm, "end": v(638.18, 28.77) * mm});
            skLineSegment(sketch, "E71.41.0.1", {"start": v(639.76, 23.98) * mm, "end": v(638.18, 28.77) * mm});
            skArc(sketch, "E71.41.0.2", {"start": v(639.76, 23.98) * mm, "mid": v(640, 23) * mm, "end": v(640.08, 22) * mm});
            skLineSegment(sketch, "E71.41.0.3", {"start": v(640.08, 19.05) * mm, "end": v(640.08, 22) * mm});
            skLineSegment(sketch, "E71.41.0.4", {"start": v(640.08, 19.05) * mm, "end": v(632.46, 19.05) * mm});
            skLineSegment(sketch, "E71.41.0.5", {"start": v(637.58, 29.21) * mm, "end": v(636.27, 29.21) * mm});
            skLineSegment(sketch, "E71.41.0.6", {"start": v(634.96, 29.2) * mm, "end": v(636.27, 29.2) * mm});
            skArc(sketch, "E71.41.0.7", {"start": v(634.96, 29.21) * mm, "mid": v(634.6, 29.09) * mm, "end": v(634.36, 28.77) * mm});
            skLineSegment(sketch, "E71.41.0.8", {"start": v(632.78, 23.98) * mm, "end": v(634.36, 28.77) * mm});
            skArc(sketch, "E71.41.0.9", {"start": v(632.78, 23.98) * mm, "mid": v(632.54, 23) * mm, "end": v(632.46, 22) * mm});
            skLineSegment(sketch, "E71.41.0.10", {"start": v(632.46, 19.05) * mm, "end": v(632.46, 22) * mm});
            skArc(sketch, "E71.42.0.0", {"start": v(652.82, 29.21) * mm, "mid": v(653.19, 29.09) * mm, "end": v(653.42, 28.77) * mm});
            skLineSegment(sketch, "E71.42.0.1", {"start": v(655, 23.98) * mm, "end": v(653.42, 28.77) * mm});
            skArc(sketch, "E71.42.0.2", {"start": v(655, 23.98) * mm, "mid": v(655.24, 23) * mm, "end": v(655.32, 22) * mm});
            skLineSegment(sketch, "E71.42.0.3", {"start": v(655.32, 19.05) * mm, "end": v(655.32, 22) * mm});
            skLineSegment(sketch, "E71.42.0.4", {"start": v(655.32, 19.05) * mm, "end": v(647.7, 19.05) * mm});
            skLineSegment(sketch, "E71.42.0.5", {"start": v(652.82, 29.21) * mm, "end": v(651.5, 29.21) * mm});
            skLineSegment(sketch, "E71.42.0.6", {"start": v(650.2, 29.2) * mm, "end": v(651.5, 29.2) * mm});
            skArc(sketch, "E71.42.0.7", {"start": v(650.2, 29.21) * mm, "mid": v(649.83, 29.09) * mm, "end": v(649.6, 28.77) * mm});
            skLineSegment(sketch, "E71.42.0.8", {"start": v(648.02, 23.98) * mm, "end": v(649.6, 28.77) * mm});
            skArc(sketch, "E71.42.0.9", {"start": v(648.02, 23.98) * mm, "mid": v(647.78, 23) * mm, "end": v(647.7, 22) * mm});
            skLineSegment(sketch, "E71.42.0.10", {"start": v(647.7, 19.05) * mm, "end": v(647.7, 22) * mm});
            skArc(sketch, "E71.43.0.0", {"start": v(668.06, 29.21) * mm, "mid": v(668.43, 29.09) * mm, "end": v(668.66, 28.77) * mm});
            skLineSegment(sketch, "E71.43.0.1", {"start": v(670.24, 23.98) * mm, "end": v(668.66, 28.77) * mm});
            skArc(sketch, "E71.43.0.2", {"start": v(670.24, 23.98) * mm, "mid": v(670.48, 23) * mm, "end": v(670.56, 22) * mm});
            skLineSegment(sketch, "E71.43.0.3", {"start": v(670.56, 19.05) * mm, "end": v(670.56, 22) * mm});
            skLineSegment(sketch, "E71.43.0.4", {"start": v(670.56, 19.05) * mm, "end": v(662.94, 19.05) * mm});
            skLineSegment(sketch, "E71.43.0.5", {"start": v(668.06, 29.21) * mm, "end": v(666.75, 29.21) * mm});
            skLineSegment(sketch, "E71.43.0.6", {"start": v(665.44, 29.2) * mm, "end": v(666.75, 29.2) * mm});
            skArc(sketch, "E71.43.0.7", {"start": v(665.44, 29.21) * mm, "mid": v(665.07, 29.09) * mm, "end": v(664.84, 28.77) * mm});
            skLineSegment(sketch, "E71.43.0.8", {"start": v(663.26, 23.98) * mm, "end": v(664.84, 28.77) * mm});
            skArc(sketch, "E71.43.0.9", {"start": v(663.26, 23.98) * mm, "mid": v(663.02, 23) * mm, "end": v(662.94, 22) * mm});
            skLineSegment(sketch, "E71.43.0.10", {"start": v(662.94, 19.05) * mm, "end": v(662.94, 22) * mm});
            skArc(sketch, "E71.44.0.0", {"start": v(683.3, 29.21) * mm, "mid": v(683.67, 29.09) * mm, "end": v(683.9, 28.77) * mm});
            skLineSegment(sketch, "E71.44.0.1", {"start": v(685.48, 23.98) * mm, "end": v(683.9, 28.77) * mm});
            skArc(sketch, "E71.44.0.2", {"start": v(685.48, 23.98) * mm, "mid": v(685.72, 23) * mm, "end": v(685.8, 22) * mm});
            skLineSegment(sketch, "E71.44.0.3", {"start": v(685.8, 19.05) * mm, "end": v(685.8, 22) * mm});
            skLineSegment(sketch, "E71.44.0.4", {"start": v(685.8, 19.05) * mm, "end": v(678.18, 19.05) * mm});
            skLineSegment(sketch, "E71.44.0.5", {"start": v(683.3, 29.21) * mm, "end": v(682, 29.21) * mm});
            skLineSegment(sketch, "E71.44.0.6", {"start": v(680.68, 29.2) * mm, "end": v(682, 29.2) * mm});
            skArc(sketch, "E71.44.0.7", {"start": v(680.68, 29.21) * mm, "mid": v(680.31, 29.09) * mm, "end": v(680.08, 28.77) * mm});
            skLineSegment(sketch, "E71.44.0.8", {"start": v(678.5, 23.98) * mm, "end": v(680.08, 28.77) * mm});
            skArc(sketch, "E71.44.0.9", {"start": v(678.5, 23.98) * mm, "mid": v(678.26, 23) * mm, "end": v(678.18, 22) * mm});
            skLineSegment(sketch, "E71.44.0.10", {"start": v(678.18, 19.05) * mm, "end": v(678.18, 22) * mm});
            skArc(sketch, "E71.45.0.0", {"start": v(698.54, 29.21) * mm, "mid": v(698.9, 29.09) * mm, "end": v(699.14, 28.77) * mm});
            skLineSegment(sketch, "E71.45.0.1", {"start": v(700.72, 23.98) * mm, "end": v(699.14, 28.77) * mm});
            skArc(sketch, "E71.45.0.2", {"start": v(700.72, 23.98) * mm, "mid": v(700.96, 23) * mm, "end": v(701.04, 22) * mm});
            skLineSegment(sketch, "E71.45.0.3", {"start": v(701.04, 19.05) * mm, "end": v(701.04, 22) * mm});
            skLineSegment(sketch, "E71.45.0.4", {"start": v(701.04, 19.05) * mm, "end": v(693.42, 19.05) * mm});
            skLineSegment(sketch, "E71.45.0.5", {"start": v(698.54, 29.21) * mm, "end": v(697.23, 29.21) * mm});
            skLineSegment(sketch, "E71.45.0.6", {"start": v(695.92, 29.2) * mm, "end": v(697.23, 29.2) * mm});
            skArc(sketch, "E71.45.0.7", {"start": v(695.92, 29.21) * mm, "mid": v(695.55, 29.09) * mm, "end": v(695.32, 28.77) * mm});
            skLineSegment(sketch, "E71.45.0.8", {"start": v(693.74, 23.98) * mm, "end": v(695.32, 28.77) * mm});
            skArc(sketch, "E71.45.0.9", {"start": v(693.74, 23.98) * mm, "mid": v(693.5, 23) * mm, "end": v(693.42, 22) * mm});
            skLineSegment(sketch, "E71.45.0.10", {"start": v(693.42, 19.05) * mm, "end": v(693.42, 22) * mm});
            skArc(sketch, "E71.46.0.0", {"start": v(713.78, 29.21) * mm, "mid": v(714.15, 29.09) * mm, "end": v(714.38, 28.77) * mm});
            skLineSegment(sketch, "E71.46.0.1", {"start": v(715.96, 23.98) * mm, "end": v(714.38, 28.77) * mm});
            skArc(sketch, "E71.46.0.2", {"start": v(715.96, 23.98) * mm, "mid": v(716.2, 23) * mm, "end": v(716.28, 22) * mm});
            skLineSegment(sketch, "E71.46.0.3", {"start": v(716.28, 19.05) * mm, "end": v(716.28, 22) * mm});
            skLineSegment(sketch, "E71.46.0.4", {"start": v(716.28, 19.05) * mm, "end": v(708.66, 19.05) * mm});
            skLineSegment(sketch, "E71.46.0.5", {"start": v(713.78, 29.21) * mm, "end": v(712.47, 29.21) * mm});
            skLineSegment(sketch, "E71.46.0.6", {"start": v(711.16, 29.2) * mm, "end": v(712.47, 29.2) * mm});
            skArc(sketch, "E71.46.0.7", {"start": v(711.16, 29.21) * mm, "mid": v(710.8, 29.09) * mm, "end": v(710.56, 28.77) * mm});
            skLineSegment(sketch, "E71.46.0.8", {"start": v(708.98, 23.98) * mm, "end": v(710.56, 28.77) * mm});
            skArc(sketch, "E71.46.0.9", {"start": v(708.98, 23.98) * mm, "mid": v(708.74, 23) * mm, "end": v(708.66, 22) * mm});
            skLineSegment(sketch, "E71.46.0.10", {"start": v(708.66, 19.05) * mm, "end": v(708.66, 22) * mm});
            skArc(sketch, "E71.47.0.0", {"start": v(729.02, 29.21) * mm, "mid": v(729.39, 29.09) * mm, "end": v(729.62, 28.77) * mm});
            skLineSegment(sketch, "E71.47.0.1", {"start": v(731.2, 23.98) * mm, "end": v(729.62, 28.77) * mm});
            skArc(sketch, "E71.47.0.2", {"start": v(731.2, 23.98) * mm, "mid": v(731.44, 23) * mm, "end": v(731.52, 22) * mm});
            skLineSegment(sketch, "E71.47.0.3", {"start": v(731.52, 19.05) * mm, "end": v(731.52, 22) * mm});
            skLineSegment(sketch, "E71.47.0.4", {"start": v(731.52, 19.05) * mm, "end": v(723.9, 19.05) * mm});
            skLineSegment(sketch, "E71.47.0.5", {"start": v(729.02, 29.21) * mm, "end": v(727.7, 29.21) * mm});
            skLineSegment(sketch, "E71.47.0.6", {"start": v(726.4, 29.2) * mm, "end": v(727.7, 29.2) * mm});
            skArc(sketch, "E71.47.0.7", {"start": v(726.4, 29.21) * mm, "mid": v(726.03, 29.09) * mm, "end": v(725.8, 28.77) * mm});
            skLineSegment(sketch, "E71.47.0.8", {"start": v(724.22, 23.98) * mm, "end": v(725.8, 28.77) * mm});
            skArc(sketch, "E71.47.0.9", {"start": v(724.22, 23.98) * mm, "mid": v(723.98, 23) * mm, "end": v(723.9, 22) * mm});
            skLineSegment(sketch, "E71.47.0.10", {"start": v(723.9, 19.05) * mm, "end": v(723.9, 22) * mm});
            skArc(sketch, "E71.48.0.0", {"start": v(744.26, 29.21) * mm, "mid": v(744.63, 29.09) * mm, "end": v(744.86, 28.77) * mm});
            skLineSegment(sketch, "E71.48.0.1", {"start": v(746.44, 23.98) * mm, "end": v(744.86, 28.77) * mm});
            skArc(sketch, "E71.48.0.2", {"start": v(746.44, 23.98) * mm, "mid": v(746.68, 23) * mm, "end": v(746.76, 22) * mm});
            skLineSegment(sketch, "E71.48.0.3", {"start": v(746.76, 19.05) * mm, "end": v(746.76, 22) * mm});
            skLineSegment(sketch, "E71.48.0.4", {"start": v(746.76, 19.05) * mm, "end": v(739.14, 19.05) * mm});
            skLineSegment(sketch, "E71.48.0.5", {"start": v(744.26, 29.21) * mm, "end": v(742.95, 29.21) * mm});
            skLineSegment(sketch, "E71.48.0.6", {"start": v(741.64, 29.2) * mm, "end": v(742.95, 29.2) * mm});
            skArc(sketch, "E71.48.0.7", {"start": v(741.64, 29.21) * mm, "mid": v(741.27, 29.09) * mm, "end": v(741.04, 28.77) * mm});
            skLineSegment(sketch, "E71.48.0.8", {"start": v(739.46, 23.98) * mm, "end": v(741.04, 28.77) * mm});
            skArc(sketch, "E71.48.0.9", {"start": v(739.46, 23.98) * mm, "mid": v(739.22, 23) * mm, "end": v(739.14, 22) * mm});
            skLineSegment(sketch, "E71.48.0.10", {"start": v(739.14, 19.05) * mm, "end": v(739.14, 22) * mm});
            skArc(sketch, "E71.49.0.0", {"start": v(759.5, 29.21) * mm, "mid": v(759.87, 29.09) * mm, "end": v(760.1, 28.77) * mm});
            skLineSegment(sketch, "E71.49.0.1", {"start": v(761.68, 23.98) * mm, "end": v(760.1, 28.77) * mm});
            skArc(sketch, "E71.49.0.2", {"start": v(761.68, 23.98) * mm, "mid": v(761.92, 23) * mm, "end": v(762, 22) * mm});
            skLineSegment(sketch, "E71.49.0.3", {"start": v(762, 19.05) * mm, "end": v(762, 22) * mm});
            skLineSegment(sketch, "E71.49.0.4", {"start": v(762, 19.05) * mm, "end": v(754.38, 19.05) * mm});
            skLineSegment(sketch, "E71.49.0.5", {"start": v(759.5, 29.21) * mm, "end": v(758.2, 29.21) * mm});
            skLineSegment(sketch, "E71.49.0.6", {"start": v(756.88, 29.2) * mm, "end": v(758.2, 29.2) * mm});
            skArc(sketch, "E71.49.0.7", {"start": v(756.88, 29.21) * mm, "mid": v(756.51, 29.09) * mm, "end": v(756.28, 28.77) * mm});
            skLineSegment(sketch, "E71.49.0.8", {"start": v(754.7, 23.98) * mm, "end": v(756.28, 28.77) * mm});
            skArc(sketch, "E71.49.0.9", {"start": v(754.7, 23.98) * mm, "mid": v(754.46, 23) * mm, "end": v(754.38, 22) * mm});
            skLineSegment(sketch, "E71.49.0.10", {"start": v(754.38, 19.05) * mm, "end": v(754.38, 22) * mm});
            skLineSegment(sketch, "E71.direction1", {"start": v(12.74, 28.57) * mm, "end": v(27.98, 28.57) * mm, "construction": true});
            skSolve(sketch);
        }
        {
            var Q0;
            Q0 = qSketchRegion(id + "F6", true);
            extrude(context, id + "F7", {"entities" : qUnion([Q0]), "operationType" : NewBodyOperationType.ADD, "oppositeDirection" : true, "depth" : 152.4 * mm});
        }
    });
